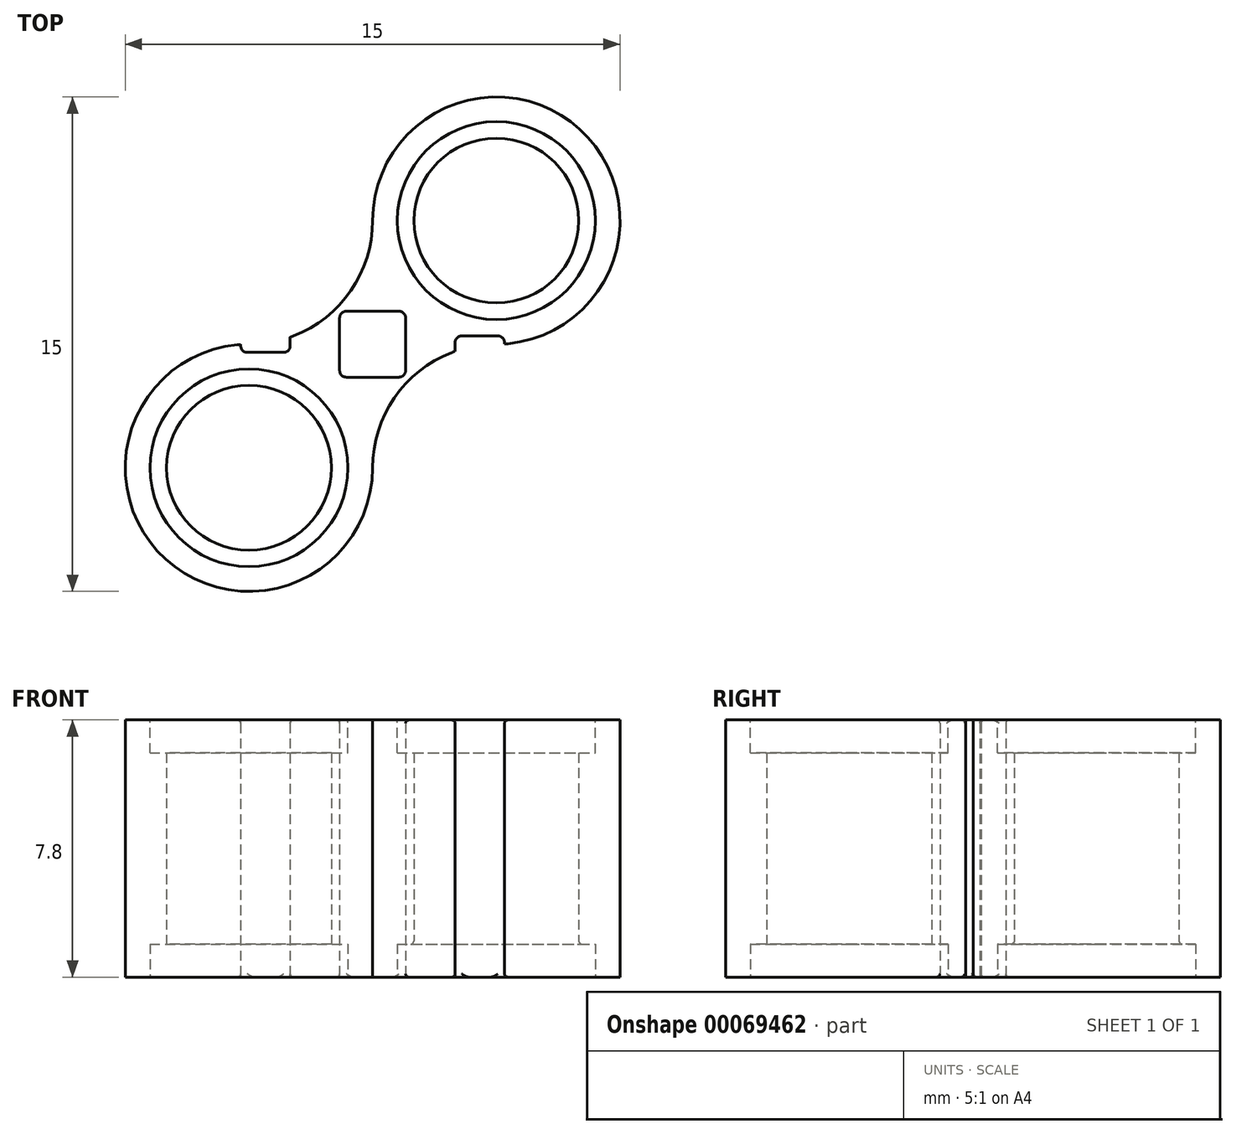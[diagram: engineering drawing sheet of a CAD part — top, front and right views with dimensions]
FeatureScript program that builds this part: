
annotation { "Feature Type Name" : "Feature", "Feature Type Description" : "" }
export const myFeature = defineFeature(function(context is Context, id is Id, definition is map)
    precondition{}
    {
        {
            var Q0;
            Q0=qCreatedBy(makeId("Top.planeOp"),FACE);
            var sketch = newSketch(context, id + "F0", { "sketchPlane" : qUnion([Q0])});
            skLineSegment(sketch, "E0.rect.bottom", {"start": v(7.5, -7.5) * mm, "end": v(-7.5, -7.5) * mm});
            skLineSegment(sketch, "E0.rect.top", {"start": v(7.5, 7.5) * mm, "end": v(-7.5, 7.5) * mm});
            skLineSegment(sketch, "E0.rect.left", {"start": v(7.5, -7.5) * mm, "end": v(7.5, 7.5) * mm});
            skLineSegment(sketch, "E0.rect.right", {"start": v(-7.5, -7.5) * mm, "end": v(-7.5, 7.5) * mm});
            skPoint(sketch, "E0.rect.middle", {"position": v(0, 0) * mm});
            skLineSegment(sketch, "E1.bottom", {"start": v(0, 0) * mm, "end": v(-7.5, 0) * mm, "construction": true});
            skLineSegment(sketch, "E1.top", {"start": v(0, 7.5) * mm, "end": v(-7.5, 7.5) * mm, "construction": true});
            skLineSegment(sketch, "E1.left", {"start": v(0, 0) * mm, "end": v(0, 7.5) * mm, "construction": true});
            skLineSegment(sketch, "E1.right", {"start": v(-7.5, 0) * mm, "end": v(-7.5, 7.5) * mm, "construction": true});
            skLineSegment(sketch, "E2.bottom", {"start": v(0, 0) * mm, "end": v(7.5, 0) * mm, "construction": true});
            skLineSegment(sketch, "E2.top", {"start": v(0, -7.5) * mm, "end": v(7.5, -7.5) * mm, "construction": true});
            skLineSegment(sketch, "E2.right", {"start": v(7.5, 0) * mm, "end": v(7.5, -7.5) * mm, "construction": true});
            skLineSegment(sketch, "E3", {"start": v(7.5, 7.5) * mm, "end": v(0, 0) * mm, "construction": true});
            skLineSegment(sketch, "E4", {"start": v(0, 0) * mm, "end": v(-7.5, -7.5) * mm, "construction": true});
            skLineSegment(sketch, "E5", {"start": v(-7.5, 7.5) * mm, "end": v(0, 0) * mm, "construction": true});
            skLineSegment(sketch, "E6", {"start": v(0, 0) * mm, "end": v(7.5, -7.5) * mm, "construction": true});
            skCircle(sketch, "E7", {"center": v(3.75, 3.75) * mm, "radius": 2.5 * mm});
            skCircle(sketch, "E8.MirrorC", {"center": v(-3.75, 3.75) * mm, "radius": 2.5 * mm});
            skCircle(sketch, "E9.MirrorC", {"center": v(-3.75, -3.75) * mm, "radius": 2.5 * mm});
            skCircle(sketch, "E10.MirrorC", {"center": v(3.75, -3.75) * mm, "radius": 2.5 * mm});
            skCircle(sketch, "E11", {"center": v(3.75, 3.75) * mm, "radius": 3.75 * mm});
            skCircle(sketch, "E12", {"center": v(3.75, 3.75) * mm, "radius": 3 * mm});
            skCircle(sketch, "E13.MirrorC", {"center": v(-3.75, 3.75) * mm, "radius": 3 * mm});
            skCircle(sketch, "E14.MirrorC", {"center": v(-3.75, 3.75) * mm, "radius": 3.75 * mm});
            skCircle(sketch, "E15.MirrorC", {"center": v(-3.75, -3.75) * mm, "radius": 3.75 * mm});
            skCircle(sketch, "E16.MirrorC", {"center": v(-3.75, -3.75) * mm, "radius": 3 * mm});
            skCircle(sketch, "E17.MirrorC", {"center": v(3.75, -3.75) * mm, "radius": 3.75 * mm});
            skCircle(sketch, "E18.MirrorC", {"center": v(3.75, -3.75) * mm, "radius": 3 * mm});
            skLineSegment(sketch, "E19.bottom", {"start": v(-3.75, 7.5) * mm, "end": v(3.75, 7.5) * mm});
            skLineSegment(sketch, "E19.top", {"start": v(-3.75, 3.75) * mm, "end": v(3.75, 3.75) * mm});
            skLineSegment(sketch, "E19.left", {"start": v(-3.75, 7.5) * mm, "end": v(-3.75, 3.75) * mm});
            skLineSegment(sketch, "E19.right", {"start": v(3.75, 7.5) * mm, "end": v(3.75, 3.75) * mm});
            skLineSegment(sketch, "E20.bottom", {"start": v(-7.5, 3.75) * mm, "end": v(-3.75, 3.75) * mm});
            skLineSegment(sketch, "E20.top", {"start": v(-7.5, -3.75) * mm, "end": v(-3.75, -3.75) * mm});
            skLineSegment(sketch, "E20.left", {"start": v(-7.5, 3.75) * mm, "end": v(-7.5, -3.75) * mm});
            skLineSegment(sketch, "E20.right", {"start": v(-3.75, 3.75) * mm, "end": v(-3.75, -3.75) * mm});
            skLineSegment(sketch, "E21.bottom", {"start": v(-3.75, -7.5) * mm, "end": v(3.75, -7.5) * mm});
            skLineSegment(sketch, "E21.top", {"start": v(-3.75, -3.75) * mm, "end": v(3.75, -3.75) * mm});
            skLineSegment(sketch, "E21.left", {"start": v(-3.75, -7.5) * mm, "end": v(-3.75, -3.75) * mm});
            skLineSegment(sketch, "E21.right", {"start": v(3.75, -7.5) * mm, "end": v(3.75, -3.75) * mm});
            skLineSegment(sketch, "E22.bottom", {"start": v(7.5, -3.75) * mm, "end": v(3.75, -3.75) * mm});
            skLineSegment(sketch, "E22.top", {"start": v(7.5, 3.75) * mm, "end": v(3.75, 3.75) * mm});
            skLineSegment(sketch, "E22.left", {"start": v(7.5, -3.75) * mm, "end": v(7.5, 3.75) * mm});
            skLineSegment(sketch, "E22.right", {"start": v(3.75, -3.75) * mm, "end": v(3.75, 3.75) * mm});
            skSolve(sketch);
        }
        {
            var Q0;
            {var subQ0=sQuery(id+"F0.wireOp",EDGE,"E19.bottom");Q0=makeQuery(id+"F0.imprint","IMPRINT",FACE,{"disambiguationData":[TD([[makeQuery(id+"F0.imprint","IMPRINT",EDGE,{"derivedFrom":subQ0}),-1.0]])]});}
            var Q1;
            {var subQ0=sQuery(id+"F0.wireOp",EDGE,"E22.left");Q1=makeQuery(id+"F0.imprint","IMPRINT",FACE,{"disambiguationData":[TD([[makeQuery(id+"F0.imprint","IMPRINT",EDGE,{"derivedFrom":subQ0}),1.0]])]});}
            var Q2;
            {var subQ0=sQuery(id+"F0.wireOp",EDGE,"E20.left");Q2=makeQuery(id+"F0.imprint","IMPRINT",FACE,{"disambiguationData":[TD([[makeQuery(id+"F0.imprint","IMPRINT",EDGE,{"derivedFrom":subQ0}),1.0]])]});}
            var Q3;
            {var subQ0=sQuery(id+"F0.wireOp",EDGE,"E21.bottom");Q3=makeQuery(id+"F0.imprint","IMPRINT",FACE,{"disambiguationData":[TD([[makeQuery(id+"F0.imprint","IMPRINT",EDGE,{"derivedFrom":subQ0}),1.0]])]});}
            var Q4;
            {var subQ0=sQuery(id+"F0.wireOp",EDGE,"E19.right");var subQ5=sQuery(id+"F0.wireOp",EDGE,"E12");var subQ6=makeQuery(id+"F0.imprint","INTERSECT",VERTEX,{"derivedFrom":[subQ5,subQ0]});Q4=makeQuery(id+"F0.imprint","IMPRINT",FACE,{"disambiguationData":[TD([[makeQuery(id+"F0.imprint","IMPRINT",EDGE,{"disambiguationData":[TD([[subQ6,1.0]])],"derivedFrom":subQ5}),-1.0]])]});}
            var Q5;
            {var subQ0=sQuery(id+"F0.wireOp",EDGE,"E19.right");var subQ5=sQuery(id+"F0.wireOp",EDGE,"E12");var subQ6=makeQuery(id+"F0.imprint","INTERSECT",VERTEX,{"derivedFrom":[subQ5,subQ0]});Q5=makeQuery(id+"F0.imprint","IMPRINT",FACE,{"disambiguationData":[TD([[makeQuery(id+"F0.imprint","IMPRINT",EDGE,{"disambiguationData":[TD([[subQ6,-1.0]])],"derivedFrom":subQ5}),-1.0]])]});}
            var Q6;
            {var subQ0=sQuery(id+"F0.wireOp",EDGE,"E22.top");var subQ5=sQuery(id+"F0.wireOp",EDGE,"E12");var subQ7=makeQuery(id+"F0.imprint","INTERSECT",VERTEX,{"derivedFrom":[subQ5,subQ0]});Q6=makeQuery(id+"F0.imprint","IMPRINT",FACE,{"disambiguationData":[TD([[makeQuery(id+"F0.imprint","IMPRINT",EDGE,{"disambiguationData":[TD([[subQ7,1.0]])],"derivedFrom":subQ5}),-1.0]])]});}
            var Q7;
            {var subQ0=sQuery(id+"F0.wireOp",EDGE,"E19.left");var subQ1=sQuery(id+"F0.wireOp",EDGE,"E13.MirrorC");var subQ2=makeQuery(id+"F0.imprint","INTERSECT",VERTEX,{"derivedFrom":[subQ1,subQ0]});Q7=makeQuery(id+"F0.imprint","IMPRINT",FACE,{"disambiguationData":[TD([[makeQuery(id+"F0.imprint","IMPRINT",EDGE,{"disambiguationData":[TD([[subQ2,1.0]])],"derivedFrom":subQ1}),1.0]])]});}
            var Q8;
            {var subQ0=sQuery(id+"F0.wireOp",EDGE,"E19.left");var subQ1=sQuery(id+"F0.wireOp",EDGE,"E13.MirrorC");var subQ2=makeQuery(id+"F0.imprint","INTERSECT",VERTEX,{"derivedFrom":[subQ1,subQ0]});Q8=makeQuery(id+"F0.imprint","IMPRINT",FACE,{"disambiguationData":[TD([[makeQuery(id+"F0.imprint","IMPRINT",EDGE,{"disambiguationData":[TD([[subQ2,-1.0]])],"derivedFrom":subQ1}),1.0]])]});}
            var Q9;
            {var subQ0=sQuery(id+"F0.wireOp",EDGE,"E20.bottom");var subQ1=sQuery(id+"F0.wireOp",EDGE,"E13.MirrorC");var subQ2=makeQuery(id+"F0.imprint","INTERSECT",VERTEX,{"derivedFrom":[subQ1,subQ0]});Q9=makeQuery(id+"F0.imprint","IMPRINT",FACE,{"disambiguationData":[TD([[makeQuery(id+"F0.imprint","IMPRINT",EDGE,{"disambiguationData":[TD([[subQ2,1.0]])],"derivedFrom":subQ1}),1.0]])]});}
            var Q10;
            {var subQ3=sQuery(id+"F0.wireOp",EDGE,"E21.left");var subQ5=sQuery(id+"F0.wireOp",EDGE,"E16.MirrorC");var subQ6=makeQuery(id+"F0.imprint","INTERSECT",VERTEX,{"derivedFrom":[subQ5,subQ3]});Q10=makeQuery(id+"F0.imprint","IMPRINT",FACE,{"disambiguationData":[TD([[makeQuery(id+"F0.imprint","IMPRINT",EDGE,{"disambiguationData":[TD([[subQ6,1.0]])],"derivedFrom":subQ5}),-1.0]])]});}
            var Q11;
            {var subQ0=sQuery(id+"F0.wireOp",EDGE,"E21.left");var subQ5=sQuery(id+"F0.wireOp",EDGE,"E16.MirrorC");var subQ6=makeQuery(id+"F0.imprint","INTERSECT",VERTEX,{"derivedFrom":[subQ5,subQ0]});Q11=makeQuery(id+"F0.imprint","IMPRINT",FACE,{"disambiguationData":[TD([[makeQuery(id+"F0.imprint","IMPRINT",EDGE,{"disambiguationData":[TD([[subQ6,-1.0]])],"derivedFrom":subQ5}),-1.0]])]});}
            var Q12;
            {var subQ0=sQuery(id+"F0.wireOp",EDGE,"E20.top");var subQ5=sQuery(id+"F0.wireOp",EDGE,"E16.MirrorC");var subQ6=makeQuery(id+"F0.imprint","INTERSECT",VERTEX,{"derivedFrom":[subQ5,subQ0]});Q12=makeQuery(id+"F0.imprint","IMPRINT",FACE,{"disambiguationData":[TD([[makeQuery(id+"F0.imprint","IMPRINT",EDGE,{"disambiguationData":[TD([[subQ6,1.0]])],"derivedFrom":subQ5}),-1.0]])]});}
            var Q13;
            {var subQ0=sQuery(id+"F0.wireOp",EDGE,"E21.right");var subQ5=sQuery(id+"F0.wireOp",EDGE,"E18.MirrorC");var subQ6=makeQuery(id+"F0.imprint","INTERSECT",VERTEX,{"derivedFrom":[subQ5,subQ0]});Q13=makeQuery(id+"F0.imprint","IMPRINT",FACE,{"disambiguationData":[TD([[makeQuery(id+"F0.imprint","IMPRINT",EDGE,{"disambiguationData":[TD([[subQ6,1.0]])],"derivedFrom":subQ5}),1.0]])]});}
            var Q14;
            {var subQ0=sQuery(id+"F0.wireOp",EDGE,"E21.right");var subQ5=sQuery(id+"F0.wireOp",EDGE,"E18.MirrorC");var subQ6=makeQuery(id+"F0.imprint","INTERSECT",VERTEX,{"derivedFrom":[subQ5,subQ0]});Q14=makeQuery(id+"F0.imprint","IMPRINT",FACE,{"disambiguationData":[TD([[makeQuery(id+"F0.imprint","IMPRINT",EDGE,{"disambiguationData":[TD([[subQ6,-1.0]])],"derivedFrom":subQ5}),1.0]])]});}
            var Q15;
            {var subQ0=sQuery(id+"F0.wireOp",EDGE,"E22.bottom");var subQ5=sQuery(id+"F0.wireOp",EDGE,"E18.MirrorC");var subQ6=makeQuery(id+"F0.imprint","INTERSECT",VERTEX,{"derivedFrom":[subQ5,subQ0]});Q15=makeQuery(id+"F0.imprint","IMPRINT",FACE,{"disambiguationData":[TD([[makeQuery(id+"F0.imprint","IMPRINT",EDGE,{"disambiguationData":[TD([[subQ6,1.0]])],"derivedFrom":subQ5}),1.0]])]});}
            var Q16;
            {var subQ0=sQuery(id+"F0.wireOp",EDGE,"E19.right");var subQ1=sQuery(id+"F0.wireOp",EDGE,"E7");var subQ2=makeQuery(id+"F0.imprint","INTERSECT",VERTEX,{"derivedFrom":[subQ1,subQ0]});Q16=makeQuery(id+"F0.imprint","IMPRINT",FACE,{"disambiguationData":[TD([[makeQuery(id+"F0.imprint","IMPRINT",EDGE,{"disambiguationData":[TD([[subQ2,1.0]])],"derivedFrom":subQ1}),-1.0]])]});}
            var Q17;
            {var subQ0=sQuery(id+"F0.wireOp",EDGE,"E22.top");var subQ1=sQuery(id+"F0.wireOp",EDGE,"E7");var subQ2=makeQuery(id+"F0.imprint","INTERSECT",VERTEX,{"derivedFrom":[subQ1,subQ0]});Q17=makeQuery(id+"F0.imprint","IMPRINT",FACE,{"disambiguationData":[TD([[makeQuery(id+"F0.imprint","IMPRINT",EDGE,{"disambiguationData":[TD([[subQ2,1.0]])],"derivedFrom":subQ1}),-1.0]])]});}
            var Q18;
            {var subQ0=sQuery(id+"F0.wireOp",EDGE,"E19.top");var subQ1=sQuery(id+"F0.wireOp",EDGE,"E7");var subQ2=makeQuery(id+"F0.imprint","INTERSECT",VERTEX,{"derivedFrom":[subQ1,subQ0]});Q18=makeQuery(id+"F0.imprint","IMPRINT",FACE,{"disambiguationData":[TD([[makeQuery(id+"F0.imprint","IMPRINT",EDGE,{"disambiguationData":[TD([[subQ2,-1.0]])],"derivedFrom":subQ1}),-1.0]])]});}
            var Q19;
            {var subQ0=sQuery(id+"F0.wireOp",EDGE,"E19.right");var subQ1=sQuery(id+"F0.wireOp",EDGE,"E7");var subQ2=makeQuery(id+"F0.imprint","INTERSECT",VERTEX,{"derivedFrom":[subQ1,subQ0]});Q19=makeQuery(id+"F0.imprint","IMPRINT",FACE,{"disambiguationData":[TD([[makeQuery(id+"F0.imprint","IMPRINT",EDGE,{"disambiguationData":[TD([[subQ2,-1.0]])],"derivedFrom":subQ1}),-1.0]])]});}
            var Q20;
            {var subQ0=sQuery(id+"F0.wireOp",EDGE,"E19.top");var subQ5=sQuery(id+"F0.wireOp",EDGE,"E12");var subQ6=makeQuery(id+"F0.imprint","INTERSECT",VERTEX,{"derivedFrom":[subQ5,subQ0]});Q20=makeQuery(id+"F0.imprint","IMPRINT",FACE,{"disambiguationData":[TD([[makeQuery(id+"F0.imprint","IMPRINT",EDGE,{"disambiguationData":[TD([[subQ6,-1.0]])],"derivedFrom":subQ5}),-1.0]])]});}
            var Q21;
            {var subQ0=sQuery(id+"F0.wireOp",EDGE,"E14.MirrorC");var subQ1=sQuery(id+"F0.wireOp",EDGE,"E11");var subQ2=makeQuery(id+"F0.imprint","INTERSECT",VERTEX,{"derivedFrom":[subQ1,subQ0,sQuery(id+"F0.wireOp",EDGE,"E19.top")]});Q21=makeQuery(id+"F0.imprint","IMPRINT",FACE,{"disambiguationData":[TD([[makeQuery(id+"F0.imprint","IMPRINT",EDGE,{"disambiguationData":[TD([[subQ2,-1.0]])],"derivedFrom":subQ1}),-1.0]])]});}
            var Q22;
            {var subQ0=sQuery(id+"F0.wireOp",EDGE,"E20.bottom");var subQ1=sQuery(id+"F0.wireOp",EDGE,"E8.MirrorC");var subQ2=makeQuery(id+"F0.imprint","INTERSECT",VERTEX,{"derivedFrom":[subQ1,subQ0]});Q22=makeQuery(id+"F0.imprint","IMPRINT",FACE,{"disambiguationData":[TD([[makeQuery(id+"F0.imprint","IMPRINT",EDGE,{"disambiguationData":[TD([[subQ2,1.0]])],"derivedFrom":subQ1}),1.0]])]});}
            var Q23;
            {var subQ0=sQuery(id+"F0.wireOp",EDGE,"E19.left");var subQ1=sQuery(id+"F0.wireOp",EDGE,"E8.MirrorC");var subQ2=makeQuery(id+"F0.imprint","INTERSECT",VERTEX,{"derivedFrom":[subQ1,subQ0]});Q23=makeQuery(id+"F0.imprint","IMPRINT",FACE,{"disambiguationData":[TD([[makeQuery(id+"F0.imprint","IMPRINT",EDGE,{"disambiguationData":[TD([[subQ2,1.0]])],"derivedFrom":subQ1}),1.0]])]});}
            var Q24;
            {var subQ0=sQuery(id+"F0.wireOp",EDGE,"E19.left");var subQ1=sQuery(id+"F0.wireOp",EDGE,"E8.MirrorC");var subQ2=makeQuery(id+"F0.imprint","INTERSECT",VERTEX,{"derivedFrom":[subQ1,subQ0]});Q24=makeQuery(id+"F0.imprint","IMPRINT",FACE,{"disambiguationData":[TD([[makeQuery(id+"F0.imprint","IMPRINT",EDGE,{"disambiguationData":[TD([[subQ2,-1.0]])],"derivedFrom":subQ1}),1.0]])]});}
            var Q25;
            {var subQ0=sQuery(id+"F0.wireOp",EDGE,"E19.top");var subQ1=sQuery(id+"F0.wireOp",EDGE,"E8.MirrorC");var subQ2=makeQuery(id+"F0.imprint","INTERSECT",VERTEX,{"derivedFrom":[subQ1,subQ0]});Q25=makeQuery(id+"F0.imprint","IMPRINT",FACE,{"disambiguationData":[TD([[makeQuery(id+"F0.imprint","IMPRINT",EDGE,{"disambiguationData":[TD([[subQ2,-1.0]])],"derivedFrom":subQ1}),1.0]])]});}
            var Q26;
            {var subQ0=sQuery(id+"F0.wireOp",EDGE,"E19.top");var subQ1=sQuery(id+"F0.wireOp",EDGE,"E13.MirrorC");var subQ2=makeQuery(id+"F0.imprint","INTERSECT",VERTEX,{"derivedFrom":[subQ1,subQ0]});Q26=makeQuery(id+"F0.imprint","IMPRINT",FACE,{"disambiguationData":[TD([[makeQuery(id+"F0.imprint","IMPRINT",EDGE,{"disambiguationData":[TD([[subQ2,-1.0]])],"derivedFrom":subQ1}),1.0]])]});}
            var Q27;
            {var subQ3=sQuery(id+"F0.wireOp",EDGE,"E21.top");var subQ5=sQuery(id+"F0.wireOp",EDGE,"E18.MirrorC");var subQ6=makeQuery(id+"F0.imprint","INTERSECT",VERTEX,{"derivedFrom":[subQ5,subQ3]});Q27=makeQuery(id+"F0.imprint","IMPRINT",FACE,{"disambiguationData":[TD([[makeQuery(id+"F0.imprint","IMPRINT",EDGE,{"disambiguationData":[TD([[subQ6,-1.0]])],"derivedFrom":subQ5}),1.0]])]});}
            var Q28;
            {var subQ0=sQuery(id+"F0.wireOp",EDGE,"E21.top");var subQ1=sQuery(id+"F0.wireOp",EDGE,"E10.MirrorC");var subQ2=makeQuery(id+"F0.imprint","INTERSECT",VERTEX,{"derivedFrom":[subQ1,subQ0]});Q28=makeQuery(id+"F0.imprint","IMPRINT",FACE,{"disambiguationData":[TD([[makeQuery(id+"F0.imprint","IMPRINT",EDGE,{"disambiguationData":[TD([[subQ2,-1.0]])],"derivedFrom":subQ1}),1.0]])]});}
            var Q29;
            {var subQ0=sQuery(id+"F0.wireOp",EDGE,"E21.right");var subQ1=sQuery(id+"F0.wireOp",EDGE,"E10.MirrorC");var subQ2=makeQuery(id+"F0.imprint","INTERSECT",VERTEX,{"derivedFrom":[subQ1,subQ0]});Q29=makeQuery(id+"F0.imprint","IMPRINT",FACE,{"disambiguationData":[TD([[makeQuery(id+"F0.imprint","IMPRINT",EDGE,{"disambiguationData":[TD([[subQ2,1.0]])],"derivedFrom":subQ1}),1.0]])]});}
            var Q30;
            {var subQ3=sQuery(id+"F0.wireOp",EDGE,"E21.top");var subQ5=sQuery(id+"F0.wireOp",EDGE,"E16.MirrorC");var subQ6=makeQuery(id+"F0.imprint","INTERSECT",VERTEX,{"derivedFrom":[subQ5,subQ3]});Q30=makeQuery(id+"F0.imprint","IMPRINT",FACE,{"disambiguationData":[TD([[makeQuery(id+"F0.imprint","IMPRINT",EDGE,{"disambiguationData":[TD([[subQ6,-1.0]])],"derivedFrom":subQ5}),-1.0]])]});}
            var Q31;
            {var subQ0=sQuery(id+"F0.wireOp",EDGE,"E21.top");var subQ1=sQuery(id+"F0.wireOp",EDGE,"E9.MirrorC");var subQ2=makeQuery(id+"F0.imprint","INTERSECT",VERTEX,{"derivedFrom":[subQ1,subQ0]});Q31=makeQuery(id+"F0.imprint","IMPRINT",FACE,{"disambiguationData":[TD([[makeQuery(id+"F0.imprint","IMPRINT",EDGE,{"disambiguationData":[TD([[subQ2,-1.0]])],"derivedFrom":subQ1}),-1.0]])]});}
            var Q32;
            {var subQ0=sQuery(id+"F0.wireOp",EDGE,"E20.top");var subQ1=sQuery(id+"F0.wireOp",EDGE,"E9.MirrorC");var subQ2=makeQuery(id+"F0.imprint","INTERSECT",VERTEX,{"derivedFrom":[subQ1,subQ0]});Q32=makeQuery(id+"F0.imprint","IMPRINT",FACE,{"disambiguationData":[TD([[makeQuery(id+"F0.imprint","IMPRINT",EDGE,{"disambiguationData":[TD([[subQ2,1.0]])],"derivedFrom":subQ1}),-1.0]])]});}
            var Q33;
            {var subQ0=sQuery(id+"F0.wireOp",EDGE,"E21.left");var subQ1=sQuery(id+"F0.wireOp",EDGE,"E9.MirrorC");var subQ2=makeQuery(id+"F0.imprint","INTERSECT",VERTEX,{"derivedFrom":[subQ1,subQ0]});Q33=makeQuery(id+"F0.imprint","IMPRINT",FACE,{"disambiguationData":[TD([[makeQuery(id+"F0.imprint","IMPRINT",EDGE,{"disambiguationData":[TD([[subQ2,1.0]])],"derivedFrom":subQ1}),-1.0]])]});}
            var Q34;
            {var subQ0=sQuery(id+"F0.wireOp",EDGE,"E21.left");var subQ1=sQuery(id+"F0.wireOp",EDGE,"E9.MirrorC");var subQ2=makeQuery(id+"F0.imprint","INTERSECT",VERTEX,{"derivedFrom":[subQ1,subQ0]});Q34=makeQuery(id+"F0.imprint","IMPRINT",FACE,{"disambiguationData":[TD([[makeQuery(id+"F0.imprint","IMPRINT",EDGE,{"disambiguationData":[TD([[subQ2,-1.0]])],"derivedFrom":subQ1}),-1.0]])]});}
            var Q35;
            {var subQ0=sQuery(id+"F0.wireOp",EDGE,"E21.right");var subQ1=sQuery(id+"F0.wireOp",EDGE,"E10.MirrorC");var subQ2=makeQuery(id+"F0.imprint","INTERSECT",VERTEX,{"derivedFrom":[subQ1,subQ0]});Q35=makeQuery(id+"F0.imprint","IMPRINT",FACE,{"disambiguationData":[TD([[makeQuery(id+"F0.imprint","IMPRINT",EDGE,{"disambiguationData":[TD([[subQ2,-1.0]])],"derivedFrom":subQ1}),1.0]])]});}
            var Q36;
            {var subQ0=sQuery(id+"F0.wireOp",EDGE,"E22.bottom");var subQ1=sQuery(id+"F0.wireOp",EDGE,"E10.MirrorC");var subQ2=makeQuery(id+"F0.imprint","INTERSECT",VERTEX,{"derivedFrom":[subQ1,subQ0]});Q36=makeQuery(id+"F0.imprint","IMPRINT",FACE,{"disambiguationData":[TD([[makeQuery(id+"F0.imprint","IMPRINT",EDGE,{"disambiguationData":[TD([[subQ2,1.0]])],"derivedFrom":subQ1}),1.0]])]});}
            extrude(context, id + "F1", {"entities" : qUnion([Q0, Q1, Q2, Q3, Q4, Q5, Q6, Q7, Q8, Q9, Q10, Q11, Q12, Q13, Q14, Q15, Q16, Q17, Q18, Q19, Q20, Q21, Q22, Q23, Q24, Q25, Q26, Q27, Q28, Q29, Q30, Q31, Q32, Q33, Q34, Q35, Q36]), "depth" : 7.8 * mm});
        }
        {
            var Q0;
            Q0=makeQuery(id+"F1.opExtrude","CAP_FACE",FACE,{"disambiguationData":[OSD([sQuery(id+"F0.wireOp",EDGE,"E7"),sQuery(id+"F0.wireOp",EDGE,"E8.MirrorC"),sQuery(id+"F0.wireOp",EDGE,"E9.MirrorC"),sQuery(id+"F0.wireOp",EDGE,"E10.MirrorC"),sQuery(id+"F0.wireOp",EDGE,"E11"),sQuery(id+"F0.wireOp",EDGE,"E14.MirrorC"),sQuery(id+"F0.wireOp",EDGE,"E15.MirrorC"),sQuery(id+"F0.wireOp",EDGE,"E17.MirrorC"),sQuery(id+"F0.wireOp",EDGE,"E19.bottom"),sQuery(id+"F0.wireOp",EDGE,"E20.left"),sQuery(id+"F0.wireOp",EDGE,"E21.bottom"),sQuery(id+"F0.wireOp",EDGE,"E22.left")])],"isStart":true});
            var sketch = newSketch(context, id + "F2", { "sketchPlane" : qUnion([Q0])});
            skCircle(sketch, "E23.0", {"center": v(-3.75, 3.75) * mm, "radius": 2.5 * mm});
            skCircle(sketch, "E24.0", {"center": v(-3.75, 3.75) * mm, "radius": 3 * mm});
            skLineSegment(sketch, "E25", {"start": v(0, 0) * mm, "end": v(-7.5, 0) * mm, "construction": true});
            skLineSegment(sketch, "E26", {"start": v(0, 7.5) * mm, "end": v(0, -7.5) * mm, "construction": true});
            skCircle(sketch, "E27.MirrorC", {"center": v(-3.75, -3.75) * mm, "radius": 3 * mm});
            skCircle(sketch, "E28.MirrorC", {"center": v(3.75, -3.75) * mm, "radius": 3 * mm});
            skCircle(sketch, "E29.MirrorC", {"center": v(3.75, 3.75) * mm, "radius": 3 * mm});
            skSolve(sketch);
        }
        {
            var Q0;
            Q0 = qSketchRegion(id + "F2", true);
            extrude(context, id + "F3", {"entities" : qUnion([Q0]), "operationType" : NewBodyOperationType.REMOVE, "oppositeDirection" : true, "depth" : 1 * mm});
        }
        {
            var Q0;
            Q0=makeQuery(id+"F1.opExtrude","CAP_FACE",FACE,{"disambiguationData":[OSD([sQuery(id+"F0.wireOp",EDGE,"E7"),sQuery(id+"F0.wireOp",EDGE,"E8.MirrorC"),sQuery(id+"F0.wireOp",EDGE,"E9.MirrorC"),sQuery(id+"F0.wireOp",EDGE,"E10.MirrorC"),sQuery(id+"F0.wireOp",EDGE,"E11"),sQuery(id+"F0.wireOp",EDGE,"E14.MirrorC"),sQuery(id+"F0.wireOp",EDGE,"E15.MirrorC"),sQuery(id+"F0.wireOp",EDGE,"E17.MirrorC"),sQuery(id+"F0.wireOp",EDGE,"E19.bottom"),sQuery(id+"F0.wireOp",EDGE,"E20.left"),sQuery(id+"F0.wireOp",EDGE,"E21.bottom"),sQuery(id+"F0.wireOp",EDGE,"E22.left")])],"isStart":true});
            cPlane(context, id + "F4", {"entities" : qUnion([Q0]), "cplaneType" : CPlaneType.OFFSET, "offset" : 3.9 * mm, "oppositeDirection" : true, "width" : 150 * mm, "height" : 150 * mm});
        }
        {
            var Q0;
            Q0=makeQuery(id+"F1.opExtrude","SWEPT_BODY",BODY,{"disambiguationData":[OSD([sQuery(id+"F0.wireOp",EDGE,"E7"),sQuery(id+"F0.wireOp",EDGE,"E8.MirrorC"),sQuery(id+"F0.wireOp",EDGE,"E9.MirrorC"),sQuery(id+"F0.wireOp",EDGE,"E10.MirrorC"),sQuery(id+"F0.wireOp",EDGE,"E11"),sQuery(id+"F0.wireOp",EDGE,"E14.MirrorC"),sQuery(id+"F0.wireOp",EDGE,"E15.MirrorC"),sQuery(id+"F0.wireOp",EDGE,"E17.MirrorC"),sQuery(id+"F0.wireOp",EDGE,"E19.bottom"),sQuery(id+"F0.wireOp",EDGE,"E20.left"),sQuery(id+"F0.wireOp",EDGE,"E21.bottom"),sQuery(id+"F0.wireOp",EDGE,"E22.left")])]});
            var Q1;
            Q1=qCreatedBy(id+"F4.planeOp",FACE);
            mirror(context, id + "F5", {"operationType" : NewBodyOperationType.INTERSECT, "entities" : qUnion([Q0]), "mirrorPlane" : qUnion([Q1])});
        }
        {
            var Q0;
            Q0=makeQuery(id+"F1.opExtrude","CAP_FACE",FACE,{"disambiguationData":[OSD([sQuery(id+"F0.wireOp",EDGE,"E7"),sQuery(id+"F0.wireOp",EDGE,"E8.MirrorC"),sQuery(id+"F0.wireOp",EDGE,"E9.MirrorC"),sQuery(id+"F0.wireOp",EDGE,"E10.MirrorC"),sQuery(id+"F0.wireOp",EDGE,"E11"),sQuery(id+"F0.wireOp",EDGE,"E14.MirrorC"),sQuery(id+"F0.wireOp",EDGE,"E15.MirrorC"),sQuery(id+"F0.wireOp",EDGE,"E17.MirrorC"),sQuery(id+"F0.wireOp",EDGE,"E19.bottom"),sQuery(id+"F0.wireOp",EDGE,"E20.left"),sQuery(id+"F0.wireOp",EDGE,"E21.bottom"),sQuery(id+"F0.wireOp",EDGE,"E22.left")])],"isStart":true});
            var sketch = newSketch(context, id + "F6", { "sketchPlane" : qUnion([Q0])});
            skLineSegment(sketch, "E30.rect.bottom", {"start": v(2.5, -1) * mm, "end": v(-2.5, -1) * mm});
            skLineSegment(sketch, "E30.rect.top", {"start": v(2.5, 1) * mm, "end": v(-2.5, 1) * mm});
            skLineSegment(sketch, "E30.rect.left", {"start": v(2.5, -1) * mm, "end": v(2.5, 1) * mm});
            skLineSegment(sketch, "E30.rect.right", {"start": v(-2.5, -1) * mm, "end": v(-2.5, 1) * mm});
            skPoint(sketch, "E30.rect.middle", {"position": v(0, 0) * mm});
            skLineSegment(sketch, "E31.rect.bottom", {"start": v(-1, 2.5) * mm, "end": v(1, 2.5) * mm});
            skLineSegment(sketch, "E31.rect.top", {"start": v(-1, -2.5) * mm, "end": v(1, -2.5) * mm});
            skLineSegment(sketch, "E31.rect.left", {"start": v(-1, 2.5) * mm, "end": v(-1, -2.5) * mm});
            skLineSegment(sketch, "E31.rect.right", {"start": v(1, 2.5) * mm, "end": v(1, -2.5) * mm});
            skLineSegment(sketch, "E32.rect.bottom", {"start": v(4, -0.25) * mm, "end": v(-4, -0.25) * mm});
            skLineSegment(sketch, "E32.rect.top", {"start": v(4, 0.25) * mm, "end": v(-4, 0.25) * mm});
            skLineSegment(sketch, "E32.rect.left", {"start": v(4, -0.25) * mm, "end": v(4, 0.25) * mm});
            skLineSegment(sketch, "E32.rect.right", {"start": v(-4, -0.25) * mm, "end": v(-4, 0.25) * mm});
            skSolve(sketch);
        }
        {
            var Q0;
            {var subQ0=sQuery(id+"F6.wireOp",EDGE,"E30.rect.right");Q0=makeQuery(id+"F6.imprint","IMPRINT",FACE,{"disambiguationData":[TD([[makeQuery(id+"F6.imprint","IMPRINT",EDGE,{"derivedFrom":subQ0}),-1.0]])]});}
            var Q1;
            {var subQ5=sQuery(id+"F6.wireOp",EDGE,"E31.rect.bottom");Q1=makeQuery(id+"F6.imprint","IMPRINT",FACE,{"disambiguationData":[TD([[makeQuery(id+"F6.imprint","IMPRINT",EDGE,{"derivedFrom":subQ5}),-1.0]])]});}
            var Q2;
            {var subQ0=sQuery(id+"F6.wireOp",EDGE,"E30.rect.left");Q2=makeQuery(id+"F6.imprint","IMPRINT",FACE,{"disambiguationData":[TD([[makeQuery(id+"F6.imprint","IMPRINT",EDGE,{"derivedFrom":subQ0}),1.0]])]});}
            var Q3;
            {var subQ5=sQuery(id+"F6.wireOp",EDGE,"E31.rect.top");Q3=makeQuery(id+"F6.imprint","IMPRINT",FACE,{"disambiguationData":[TD([[makeQuery(id+"F6.imprint","IMPRINT",EDGE,{"derivedFrom":subQ5}),1.0]])]});}
            var Q4;
            {var subQ0=sQuery(id+"F6.wireOp",EDGE,"E31.rect.right");var subQ1=sQuery(id+"F6.wireOp",EDGE,"E30.rect.bottom");var subQ2=makeQuery(id+"F6.imprint","INTERSECT",VERTEX,{"derivedFrom":[subQ1,subQ0]});Q4=makeQuery(id+"F6.imprint","IMPRINT",FACE,{"disambiguationData":[TD([[makeQuery(id+"F6.imprint","IMPRINT",EDGE,{"disambiguationData":[TD([[subQ2,-1.0]])],"derivedFrom":subQ1}),-1.0]])]});}
            var Q5;
            {var subQ5=sQuery(id+"F6.wireOp",EDGE,"E32.rect.left");Q5=makeQuery(id+"F6.imprint","IMPRINT",FACE,{"disambiguationData":[TD([[makeQuery(id+"F6.imprint","IMPRINT",EDGE,{"derivedFrom":subQ5}),1.0]])]});}
            var Q6;
            {var subQ0=sQuery(id+"F6.wireOp",EDGE,"E32.rect.top");var subQ1=sQuery(id+"F6.wireOp",EDGE,"E31.rect.left");var subQ2=makeQuery(id+"F6.imprint","INTERSECT",VERTEX,{"derivedFrom":[subQ1,subQ0]});Q6=makeQuery(id+"F6.imprint","IMPRINT",FACE,{"disambiguationData":[TD([[makeQuery(id+"F6.imprint","IMPRINT",EDGE,{"disambiguationData":[TD([[subQ2,-1.0]])],"derivedFrom":subQ1}),1.0]])]});}
            var Q7;
            {var subQ5=sQuery(id+"F6.wireOp",EDGE,"E32.rect.right");Q7=makeQuery(id+"F6.imprint","IMPRINT",FACE,{"disambiguationData":[TD([[makeQuery(id+"F6.imprint","IMPRINT",EDGE,{"derivedFrom":subQ5}),-1.0]])]});}
            var Q8;
            {var subQ0=sQuery(id+"F6.wireOp",EDGE,"E31.rect.right");var subQ1=sQuery(id+"F6.wireOp",EDGE,"E30.rect.top");var subQ2=makeQuery(id+"F6.imprint","INTERSECT",VERTEX,{"derivedFrom":[subQ1,subQ0]});Q8=makeQuery(id+"F6.imprint","IMPRINT",FACE,{"disambiguationData":[TD([[makeQuery(id+"F6.imprint","IMPRINT",EDGE,{"disambiguationData":[TD([[subQ2,-1.0]])],"derivedFrom":subQ1}),1.0]])]});}
            extrude(context, id + "F7", {"entities" : qUnion([Q0, Q1, Q2, Q3, Q4, Q5, Q6, Q7, Q8]), "operationType" : NewBodyOperationType.REMOVE, "oppositeDirection" : true, "depth" : 25 * mm});
        }
        {
            var Q0;
            Q0=makeQuery(id+"F7.boolean.opBoolean","COPY",EDGE,{"derivedFrom":makeQuery(id+"F7.opExtrude","SWEPT_EDGE",EDGE,{"disambiguationData":[OSD([sQuery(id+"F6.wireOp",EDGE,"E30.rect.bottom"),sQuery(id+"F6.wireOp",EDGE,"E30.rect.left")])]})});
            var Q1;
            Q1=makeQuery(id+"F7.boolean.opBoolean","COPY",EDGE,{"derivedFrom":makeQuery(id+"F7.opExtrude","SWEPT_EDGE",EDGE,{"disambiguationData":[OSD([sQuery(id+"F6.wireOp",EDGE,"E31.rect.top"),sQuery(id+"F6.wireOp",EDGE,"E31.rect.right")])]})});
            var Q2;
            Q2=makeQuery(id+"F7.boolean.opBoolean","COPY",EDGE,{"derivedFrom":makeQuery(id+"F7.opExtrude","SWEPT_EDGE",EDGE,{"disambiguationData":[OSD([sQuery(id+"F6.wireOp",EDGE,"E30.rect.top"),sQuery(id+"F6.wireOp",EDGE,"E30.rect.left")])]})});
            var Q3;
            Q3=makeQuery(id+"F7.boolean.opBoolean","COPY",EDGE,{"derivedFrom":makeQuery(id+"F7.opExtrude","SWEPT_EDGE",EDGE,{"disambiguationData":[OSD([sQuery(id+"F6.wireOp",EDGE,"E31.rect.bottom"),sQuery(id+"F6.wireOp",EDGE,"E31.rect.right")])]})});
            var Q4;
            Q4=makeQuery(id+"F7.boolean.opBoolean","COPY",EDGE,{"derivedFrom":makeQuery(id+"F7.opExtrude","SWEPT_EDGE",EDGE,{"disambiguationData":[OSD([sQuery(id+"F6.wireOp",EDGE,"E31.rect.bottom"),sQuery(id+"F6.wireOp",EDGE,"E31.rect.left")])]})});
            var Q5;
            Q5=makeQuery(id+"F7.boolean.opBoolean","COPY",EDGE,{"derivedFrom":makeQuery(id+"F7.opExtrude","SWEPT_EDGE",EDGE,{"disambiguationData":[OSD([sQuery(id+"F6.wireOp",EDGE,"E30.rect.top"),sQuery(id+"F6.wireOp",EDGE,"E30.rect.right")])]})});
            var Q6;
            Q6=makeQuery(id+"F7.boolean.opBoolean","COPY",EDGE,{"derivedFrom":makeQuery(id+"F7.opExtrude","SWEPT_EDGE",EDGE,{"disambiguationData":[OSD([sQuery(id+"F6.wireOp",EDGE,"E30.rect.bottom"),sQuery(id+"F6.wireOp",EDGE,"E30.rect.right")])]})});
            var Q7;
            Q7=makeQuery(id+"F7.boolean.opBoolean","COPY",EDGE,{"derivedFrom":makeQuery(id+"F7.opExtrude","SWEPT_EDGE",EDGE,{"disambiguationData":[OSD([sQuery(id+"F6.wireOp",EDGE,"E31.rect.top"),sQuery(id+"F6.wireOp",EDGE,"E31.rect.left")])]})});
            var Q8;
            Q8=makeQuery(id+"F7.boolean.opBoolean","COPY",EDGE,{"derivedFrom":makeQuery(id+"F7.opExtrude","SWEPT_EDGE",EDGE,{"disambiguationData":[OSD([sQuery(id+"F6.wireOp",EDGE,"E32.rect.bottom"),sQuery(id+"F6.wireOp",EDGE,"E32.rect.right")])]})});
            var Q9;
            Q9=makeQuery(id+"F7.boolean.opBoolean","COPY",EDGE,{"derivedFrom":makeQuery(id+"F7.opExtrude","SWEPT_EDGE",EDGE,{"disambiguationData":[OSD([sQuery(id+"F6.wireOp",EDGE,"E32.rect.top"),sQuery(id+"F6.wireOp",EDGE,"E32.rect.right")])]})});
            var Q10;
            Q10=makeQuery(id+"F7.boolean.opBoolean","COPY",EDGE,{"derivedFrom":makeQuery(id+"F7.opExtrude","SWEPT_EDGE",EDGE,{"disambiguationData":[OSD([sQuery(id+"F6.wireOp",EDGE,"E32.rect.top"),sQuery(id+"F6.wireOp",EDGE,"E32.rect.left")])]})});
            var Q11;
            Q11=makeQuery(id+"F7.boolean.opBoolean","COPY",EDGE,{"derivedFrom":makeQuery(id+"F7.opExtrude","SWEPT_EDGE",EDGE,{"disambiguationData":[OSD([sQuery(id+"F6.wireOp",EDGE,"E32.rect.bottom"),sQuery(id+"F6.wireOp",EDGE,"E32.rect.left")])]})});
            fillet(context, id + "F8", {"entities" : qUnion([Q0, Q1, Q2, Q3, Q4, Q5, Q6, Q7, Q8, Q9, Q10, Q11]), "radius" : 0.2 * mm, "tangentPropagation" : true, "allowEdgeOverflow" : false});
        }
        {
            var Q0;
            Q0=makeQuery(id+"F7.boolean.opBoolean","COPY",EDGE,{"derivedFrom":makeQuery(id+"F7.opExtrude","CAP_EDGE",EDGE,{"disambiguationData":[OSD([sQuery(id+"F6.wireOp",EDGE,"E31.rect.bottom")])],"isStart":true})});
            var Q1;
            {var subQ0=sQuery(id+"F6.wireOp",EDGE,"E31.rect.left");Q1=makeQuery(id+"F7.boolean.opBoolean","COPY",EDGE,{"derivedFrom":makeQuery(id+"F7.opExtrude","CAP_EDGE",EDGE,{"disambiguationData":[OSD([subQ0]),TDD([makeQuery(id+"F6.imprint","IMPRINT",EDGE,{"disambiguationData":[TD([[makeQuery(id+"F6.imprint","INTERSECT",VERTEX,{"derivedFrom":[sQuery(id+"F6.wireOp",EDGE,"E31.rect.bottom"),subQ0]}),-1.0]])],"derivedFrom":subQ0})])],"isStart":true})});}
            var Q2;
            Q2=makeQuery(id+"F8.opFillet","BLEND_EDGE",EDGE,{"blendedFrom":[makeQuery(id+"F7.boolean.opBoolean","COPY",EDGE,{"derivedFrom":makeQuery(id+"F7.opExtrude","SWEPT_EDGE",EDGE,{"disambiguationData":[OSD([sQuery(id+"F6.wireOp",EDGE,"E31.rect.bottom"),sQuery(id+"F6.wireOp",EDGE,"E31.rect.left")])]})}),makeQuery(id+"F1.opExtrude","CAP_FACE",FACE,{"disambiguationData":[OSD([sQuery(id+"F0.wireOp",EDGE,"E7"),sQuery(id+"F0.wireOp",EDGE,"E8.MirrorC"),sQuery(id+"F0.wireOp",EDGE,"E9.MirrorC"),sQuery(id+"F0.wireOp",EDGE,"E10.MirrorC"),sQuery(id+"F0.wireOp",EDGE,"E11"),sQuery(id+"F0.wireOp",EDGE,"E14.MirrorC"),sQuery(id+"F0.wireOp",EDGE,"E15.MirrorC"),sQuery(id+"F0.wireOp",EDGE,"E17.MirrorC"),sQuery(id+"F0.wireOp",EDGE,"E19.bottom"),sQuery(id+"F0.wireOp",EDGE,"E20.left"),sQuery(id+"F0.wireOp",EDGE,"E21.bottom"),sQuery(id+"F0.wireOp",EDGE,"E22.left")])],"isStart":true})],"blendedInto":[makeQuery(id+"F1.opExtrude","CAP_FACE",FACE,{"disambiguationData":[OSD([sQuery(id+"F0.wireOp",EDGE,"E7"),sQuery(id+"F0.wireOp",EDGE,"E8.MirrorC"),sQuery(id+"F0.wireOp",EDGE,"E9.MirrorC"),sQuery(id+"F0.wireOp",EDGE,"E10.MirrorC"),sQuery(id+"F0.wireOp",EDGE,"E11"),sQuery(id+"F0.wireOp",EDGE,"E14.MirrorC"),sQuery(id+"F0.wireOp",EDGE,"E15.MirrorC"),sQuery(id+"F0.wireOp",EDGE,"E17.MirrorC"),sQuery(id+"F0.wireOp",EDGE,"E19.bottom"),sQuery(id+"F0.wireOp",EDGE,"E20.left"),sQuery(id+"F0.wireOp",EDGE,"E21.bottom"),sQuery(id+"F0.wireOp",EDGE,"E22.left")])],"isStart":true})]});
            var Q3;
            Q3=makeQuery(id+"F8.opFillet","BLEND_EDGE",EDGE,{"blendedFrom":[makeQuery(id+"F7.boolean.opBoolean","COPY",EDGE,{"derivedFrom":makeQuery(id+"F7.opExtrude","SWEPT_EDGE",EDGE,{"disambiguationData":[OSD([sQuery(id+"F6.wireOp",EDGE,"E31.rect.bottom"),sQuery(id+"F6.wireOp",EDGE,"E31.rect.right")])]})}),makeQuery(id+"F1.opExtrude","CAP_FACE",FACE,{"disambiguationData":[OSD([sQuery(id+"F0.wireOp",EDGE,"E7"),sQuery(id+"F0.wireOp",EDGE,"E8.MirrorC"),sQuery(id+"F0.wireOp",EDGE,"E9.MirrorC"),sQuery(id+"F0.wireOp",EDGE,"E10.MirrorC"),sQuery(id+"F0.wireOp",EDGE,"E11"),sQuery(id+"F0.wireOp",EDGE,"E14.MirrorC"),sQuery(id+"F0.wireOp",EDGE,"E15.MirrorC"),sQuery(id+"F0.wireOp",EDGE,"E17.MirrorC"),sQuery(id+"F0.wireOp",EDGE,"E19.bottom"),sQuery(id+"F0.wireOp",EDGE,"E20.left"),sQuery(id+"F0.wireOp",EDGE,"E21.bottom"),sQuery(id+"F0.wireOp",EDGE,"E22.left")])],"isStart":true})],"blendedInto":[makeQuery(id+"F1.opExtrude","CAP_FACE",FACE,{"disambiguationData":[OSD([sQuery(id+"F0.wireOp",EDGE,"E7"),sQuery(id+"F0.wireOp",EDGE,"E8.MirrorC"),sQuery(id+"F0.wireOp",EDGE,"E9.MirrorC"),sQuery(id+"F0.wireOp",EDGE,"E10.MirrorC"),sQuery(id+"F0.wireOp",EDGE,"E11"),sQuery(id+"F0.wireOp",EDGE,"E14.MirrorC"),sQuery(id+"F0.wireOp",EDGE,"E15.MirrorC"),sQuery(id+"F0.wireOp",EDGE,"E17.MirrorC"),sQuery(id+"F0.wireOp",EDGE,"E19.bottom"),sQuery(id+"F0.wireOp",EDGE,"E20.left"),sQuery(id+"F0.wireOp",EDGE,"E21.bottom"),sQuery(id+"F0.wireOp",EDGE,"E22.left")])],"isStart":true})]});
            var Q4;
            {var subQ0=sQuery(id+"F6.wireOp",EDGE,"E31.rect.right");Q4=makeQuery(id+"F7.boolean.opBoolean","COPY",EDGE,{"derivedFrom":makeQuery(id+"F7.opExtrude","CAP_EDGE",EDGE,{"disambiguationData":[OSD([subQ0]),TDD([makeQuery(id+"F6.imprint","IMPRINT",EDGE,{"disambiguationData":[TD([[makeQuery(id+"F6.imprint","INTERSECT",VERTEX,{"derivedFrom":[sQuery(id+"F6.wireOp",EDGE,"E31.rect.bottom"),subQ0]}),-1.0]])],"derivedFrom":subQ0})])],"isStart":true})});}
            var Q5;
            {var subQ0=sQuery(id+"F6.wireOp",EDGE,"E30.rect.top");Q5=makeQuery(id+"F7.boolean.opBoolean","COPY",EDGE,{"derivedFrom":makeQuery(id+"F7.opExtrude","CAP_EDGE",EDGE,{"disambiguationData":[OSD([subQ0]),TDD([makeQuery(id+"F6.imprint","IMPRINT",EDGE,{"disambiguationData":[TD([[makeQuery(id+"F6.imprint","INTERSECT",VERTEX,{"derivedFrom":[subQ0,sQuery(id+"F6.wireOp",EDGE,"E30.rect.left")]}),-1.0]])],"derivedFrom":subQ0})])],"isStart":true})});}
            var Q6;
            Q6=makeQuery(id+"F8.opFillet","BLEND_EDGE",EDGE,{"blendedFrom":[makeQuery(id+"F7.boolean.opBoolean","COPY",EDGE,{"derivedFrom":makeQuery(id+"F7.opExtrude","SWEPT_EDGE",EDGE,{"disambiguationData":[OSD([sQuery(id+"F6.wireOp",EDGE,"E30.rect.top"),sQuery(id+"F6.wireOp",EDGE,"E30.rect.left")])]})}),makeQuery(id+"F1.opExtrude","CAP_FACE",FACE,{"disambiguationData":[OSD([sQuery(id+"F0.wireOp",EDGE,"E7"),sQuery(id+"F0.wireOp",EDGE,"E8.MirrorC"),sQuery(id+"F0.wireOp",EDGE,"E9.MirrorC"),sQuery(id+"F0.wireOp",EDGE,"E10.MirrorC"),sQuery(id+"F0.wireOp",EDGE,"E11"),sQuery(id+"F0.wireOp",EDGE,"E14.MirrorC"),sQuery(id+"F0.wireOp",EDGE,"E15.MirrorC"),sQuery(id+"F0.wireOp",EDGE,"E17.MirrorC"),sQuery(id+"F0.wireOp",EDGE,"E19.bottom"),sQuery(id+"F0.wireOp",EDGE,"E20.left"),sQuery(id+"F0.wireOp",EDGE,"E21.bottom"),sQuery(id+"F0.wireOp",EDGE,"E22.left")])],"isStart":true})],"blendedInto":[makeQuery(id+"F1.opExtrude","CAP_FACE",FACE,{"disambiguationData":[OSD([sQuery(id+"F0.wireOp",EDGE,"E7"),sQuery(id+"F0.wireOp",EDGE,"E8.MirrorC"),sQuery(id+"F0.wireOp",EDGE,"E9.MirrorC"),sQuery(id+"F0.wireOp",EDGE,"E10.MirrorC"),sQuery(id+"F0.wireOp",EDGE,"E11"),sQuery(id+"F0.wireOp",EDGE,"E14.MirrorC"),sQuery(id+"F0.wireOp",EDGE,"E15.MirrorC"),sQuery(id+"F0.wireOp",EDGE,"E17.MirrorC"),sQuery(id+"F0.wireOp",EDGE,"E19.bottom"),sQuery(id+"F0.wireOp",EDGE,"E20.left"),sQuery(id+"F0.wireOp",EDGE,"E21.bottom"),sQuery(id+"F0.wireOp",EDGE,"E22.left")])],"isStart":true})]});
            var Q7;
            {var subQ0=sQuery(id+"F6.wireOp",EDGE,"E30.rect.left");Q7=makeQuery(id+"F7.boolean.opBoolean","COPY",EDGE,{"derivedFrom":makeQuery(id+"F7.opExtrude","CAP_EDGE",EDGE,{"disambiguationData":[OSD([subQ0]),TDD([makeQuery(id+"F6.imprint","IMPRINT",EDGE,{"disambiguationData":[TD([[makeQuery(id+"F6.imprint","INTERSECT",VERTEX,{"derivedFrom":[sQuery(id+"F6.wireOp",EDGE,"E30.rect.top"),subQ0]}),1.0]])],"derivedFrom":subQ0})])],"isStart":true})});}
            var Q8;
            {var subQ0=sQuery(id+"F6.wireOp",EDGE,"E32.rect.top");Q8=makeQuery(id+"F7.boolean.opBoolean","COPY",EDGE,{"derivedFrom":makeQuery(id+"F7.opExtrude","CAP_EDGE",EDGE,{"disambiguationData":[OSD([subQ0]),TDD([makeQuery(id+"F6.imprint","IMPRINT",EDGE,{"disambiguationData":[TD([[makeQuery(id+"F6.imprint","INTERSECT",VERTEX,{"derivedFrom":[subQ0,sQuery(id+"F6.wireOp",EDGE,"E32.rect.left")]}),-1.0]])],"derivedFrom":subQ0})])],"isStart":true})});}
            var Q9;
            Q9=makeQuery(id+"F8.opFillet","BLEND_EDGE",EDGE,{"blendedFrom":[makeQuery(id+"F7.boolean.opBoolean","COPY",EDGE,{"derivedFrom":makeQuery(id+"F7.opExtrude","SWEPT_EDGE",EDGE,{"disambiguationData":[OSD([sQuery(id+"F6.wireOp",EDGE,"E32.rect.top"),sQuery(id+"F6.wireOp",EDGE,"E32.rect.left")])]})}),makeQuery(id+"F1.opExtrude","CAP_FACE",FACE,{"disambiguationData":[OSD([sQuery(id+"F0.wireOp",EDGE,"E7"),sQuery(id+"F0.wireOp",EDGE,"E8.MirrorC"),sQuery(id+"F0.wireOp",EDGE,"E9.MirrorC"),sQuery(id+"F0.wireOp",EDGE,"E10.MirrorC"),sQuery(id+"F0.wireOp",EDGE,"E11"),sQuery(id+"F0.wireOp",EDGE,"E14.MirrorC"),sQuery(id+"F0.wireOp",EDGE,"E15.MirrorC"),sQuery(id+"F0.wireOp",EDGE,"E17.MirrorC"),sQuery(id+"F0.wireOp",EDGE,"E19.bottom"),sQuery(id+"F0.wireOp",EDGE,"E20.left"),sQuery(id+"F0.wireOp",EDGE,"E21.bottom"),sQuery(id+"F0.wireOp",EDGE,"E22.left")])],"isStart":true})],"blendedInto":[makeQuery(id+"F1.opExtrude","CAP_FACE",FACE,{"disambiguationData":[OSD([sQuery(id+"F0.wireOp",EDGE,"E7"),sQuery(id+"F0.wireOp",EDGE,"E8.MirrorC"),sQuery(id+"F0.wireOp",EDGE,"E9.MirrorC"),sQuery(id+"F0.wireOp",EDGE,"E10.MirrorC"),sQuery(id+"F0.wireOp",EDGE,"E11"),sQuery(id+"F0.wireOp",EDGE,"E14.MirrorC"),sQuery(id+"F0.wireOp",EDGE,"E15.MirrorC"),sQuery(id+"F0.wireOp",EDGE,"E17.MirrorC"),sQuery(id+"F0.wireOp",EDGE,"E19.bottom"),sQuery(id+"F0.wireOp",EDGE,"E20.left"),sQuery(id+"F0.wireOp",EDGE,"E21.bottom"),sQuery(id+"F0.wireOp",EDGE,"E22.left")])],"isStart":true})]});
            var Q10;
            Q10=makeQuery(id+"F7.boolean.opBoolean","COPY",EDGE,{"derivedFrom":makeQuery(id+"F7.opExtrude","CAP_EDGE",EDGE,{"disambiguationData":[OSD([sQuery(id+"F6.wireOp",EDGE,"E32.rect.left")])],"isStart":true})});
            var Q11;
            Q11=makeQuery(id+"F8.opFillet","BLEND_EDGE",EDGE,{"blendedFrom":[makeQuery(id+"F7.boolean.opBoolean","COPY",EDGE,{"derivedFrom":makeQuery(id+"F7.opExtrude","SWEPT_EDGE",EDGE,{"disambiguationData":[OSD([sQuery(id+"F6.wireOp",EDGE,"E32.rect.bottom"),sQuery(id+"F6.wireOp",EDGE,"E32.rect.left")])]})}),makeQuery(id+"F1.opExtrude","CAP_FACE",FACE,{"disambiguationData":[OSD([sQuery(id+"F0.wireOp",EDGE,"E7"),sQuery(id+"F0.wireOp",EDGE,"E8.MirrorC"),sQuery(id+"F0.wireOp",EDGE,"E9.MirrorC"),sQuery(id+"F0.wireOp",EDGE,"E10.MirrorC"),sQuery(id+"F0.wireOp",EDGE,"E11"),sQuery(id+"F0.wireOp",EDGE,"E14.MirrorC"),sQuery(id+"F0.wireOp",EDGE,"E15.MirrorC"),sQuery(id+"F0.wireOp",EDGE,"E17.MirrorC"),sQuery(id+"F0.wireOp",EDGE,"E19.bottom"),sQuery(id+"F0.wireOp",EDGE,"E20.left"),sQuery(id+"F0.wireOp",EDGE,"E21.bottom"),sQuery(id+"F0.wireOp",EDGE,"E22.left")])],"isStart":true})],"blendedInto":[makeQuery(id+"F1.opExtrude","CAP_FACE",FACE,{"disambiguationData":[OSD([sQuery(id+"F0.wireOp",EDGE,"E7"),sQuery(id+"F0.wireOp",EDGE,"E8.MirrorC"),sQuery(id+"F0.wireOp",EDGE,"E9.MirrorC"),sQuery(id+"F0.wireOp",EDGE,"E10.MirrorC"),sQuery(id+"F0.wireOp",EDGE,"E11"),sQuery(id+"F0.wireOp",EDGE,"E14.MirrorC"),sQuery(id+"F0.wireOp",EDGE,"E15.MirrorC"),sQuery(id+"F0.wireOp",EDGE,"E17.MirrorC"),sQuery(id+"F0.wireOp",EDGE,"E19.bottom"),sQuery(id+"F0.wireOp",EDGE,"E20.left"),sQuery(id+"F0.wireOp",EDGE,"E21.bottom"),sQuery(id+"F0.wireOp",EDGE,"E22.left")])],"isStart":true})]});
            var Q12;
            {var subQ0=sQuery(id+"F6.wireOp",EDGE,"E32.rect.bottom");Q12=makeQuery(id+"F7.boolean.opBoolean","COPY",EDGE,{"derivedFrom":makeQuery(id+"F7.opExtrude","CAP_EDGE",EDGE,{"disambiguationData":[OSD([subQ0]),TDD([makeQuery(id+"F6.imprint","IMPRINT",EDGE,{"disambiguationData":[TD([[makeQuery(id+"F6.imprint","INTERSECT",VERTEX,{"derivedFrom":[subQ0,sQuery(id+"F6.wireOp",EDGE,"E32.rect.left")]}),-1.0]])],"derivedFrom":subQ0})])],"isStart":true})});}
            var Q13;
            {var subQ0=sQuery(id+"F6.wireOp",EDGE,"E30.rect.left");Q13=makeQuery(id+"F7.boolean.opBoolean","COPY",EDGE,{"derivedFrom":makeQuery(id+"F7.opExtrude","CAP_EDGE",EDGE,{"disambiguationData":[OSD([subQ0]),TDD([makeQuery(id+"F6.imprint","IMPRINT",EDGE,{"disambiguationData":[TD([[makeQuery(id+"F6.imprint","INTERSECT",VERTEX,{"derivedFrom":[sQuery(id+"F6.wireOp",EDGE,"E30.rect.bottom"),subQ0]}),-1.0]])],"derivedFrom":subQ0})])],"isStart":true})});}
            var Q14;
            Q14=makeQuery(id+"F8.opFillet","BLEND_EDGE",EDGE,{"blendedFrom":[makeQuery(id+"F7.boolean.opBoolean","COPY",EDGE,{"derivedFrom":makeQuery(id+"F7.opExtrude","SWEPT_EDGE",EDGE,{"disambiguationData":[OSD([sQuery(id+"F6.wireOp",EDGE,"E30.rect.bottom"),sQuery(id+"F6.wireOp",EDGE,"E30.rect.left")])]})}),makeQuery(id+"F1.opExtrude","CAP_FACE",FACE,{"disambiguationData":[OSD([sQuery(id+"F0.wireOp",EDGE,"E7"),sQuery(id+"F0.wireOp",EDGE,"E8.MirrorC"),sQuery(id+"F0.wireOp",EDGE,"E9.MirrorC"),sQuery(id+"F0.wireOp",EDGE,"E10.MirrorC"),sQuery(id+"F0.wireOp",EDGE,"E11"),sQuery(id+"F0.wireOp",EDGE,"E14.MirrorC"),sQuery(id+"F0.wireOp",EDGE,"E15.MirrorC"),sQuery(id+"F0.wireOp",EDGE,"E17.MirrorC"),sQuery(id+"F0.wireOp",EDGE,"E19.bottom"),sQuery(id+"F0.wireOp",EDGE,"E20.left"),sQuery(id+"F0.wireOp",EDGE,"E21.bottom"),sQuery(id+"F0.wireOp",EDGE,"E22.left")])],"isStart":true})],"blendedInto":[makeQuery(id+"F1.opExtrude","CAP_FACE",FACE,{"disambiguationData":[OSD([sQuery(id+"F0.wireOp",EDGE,"E7"),sQuery(id+"F0.wireOp",EDGE,"E8.MirrorC"),sQuery(id+"F0.wireOp",EDGE,"E9.MirrorC"),sQuery(id+"F0.wireOp",EDGE,"E10.MirrorC"),sQuery(id+"F0.wireOp",EDGE,"E11"),sQuery(id+"F0.wireOp",EDGE,"E14.MirrorC"),sQuery(id+"F0.wireOp",EDGE,"E15.MirrorC"),sQuery(id+"F0.wireOp",EDGE,"E17.MirrorC"),sQuery(id+"F0.wireOp",EDGE,"E19.bottom"),sQuery(id+"F0.wireOp",EDGE,"E20.left"),sQuery(id+"F0.wireOp",EDGE,"E21.bottom"),sQuery(id+"F0.wireOp",EDGE,"E22.left")])],"isStart":true})]});
            var Q15;
            {var subQ0=sQuery(id+"F6.wireOp",EDGE,"E30.rect.bottom");Q15=makeQuery(id+"F7.boolean.opBoolean","COPY",EDGE,{"derivedFrom":makeQuery(id+"F7.opExtrude","CAP_EDGE",EDGE,{"disambiguationData":[OSD([subQ0]),TDD([makeQuery(id+"F6.imprint","IMPRINT",EDGE,{"disambiguationData":[TD([[makeQuery(id+"F6.imprint","INTERSECT",VERTEX,{"derivedFrom":[subQ0,sQuery(id+"F6.wireOp",EDGE,"E30.rect.left")]}),-1.0]])],"derivedFrom":subQ0})])],"isStart":true})});}
            var Q16;
            {var subQ0=sQuery(id+"F6.wireOp",EDGE,"E31.rect.right");Q16=makeQuery(id+"F7.boolean.opBoolean","COPY",EDGE,{"derivedFrom":makeQuery(id+"F7.opExtrude","CAP_EDGE",EDGE,{"disambiguationData":[OSD([subQ0]),TDD([makeQuery(id+"F6.imprint","IMPRINT",EDGE,{"disambiguationData":[TD([[makeQuery(id+"F6.imprint","INTERSECT",VERTEX,{"derivedFrom":[sQuery(id+"F6.wireOp",EDGE,"E31.rect.top"),subQ0]}),1.0]])],"derivedFrom":subQ0})])],"isStart":true})});}
            var Q17;
            Q17=makeQuery(id+"F8.opFillet","BLEND_EDGE",EDGE,{"blendedFrom":[makeQuery(id+"F7.boolean.opBoolean","COPY",EDGE,{"derivedFrom":makeQuery(id+"F7.opExtrude","SWEPT_EDGE",EDGE,{"disambiguationData":[OSD([sQuery(id+"F6.wireOp",EDGE,"E31.rect.top"),sQuery(id+"F6.wireOp",EDGE,"E31.rect.right")])]})}),makeQuery(id+"F1.opExtrude","CAP_FACE",FACE,{"disambiguationData":[OSD([sQuery(id+"F0.wireOp",EDGE,"E7"),sQuery(id+"F0.wireOp",EDGE,"E8.MirrorC"),sQuery(id+"F0.wireOp",EDGE,"E9.MirrorC"),sQuery(id+"F0.wireOp",EDGE,"E10.MirrorC"),sQuery(id+"F0.wireOp",EDGE,"E11"),sQuery(id+"F0.wireOp",EDGE,"E14.MirrorC"),sQuery(id+"F0.wireOp",EDGE,"E15.MirrorC"),sQuery(id+"F0.wireOp",EDGE,"E17.MirrorC"),sQuery(id+"F0.wireOp",EDGE,"E19.bottom"),sQuery(id+"F0.wireOp",EDGE,"E20.left"),sQuery(id+"F0.wireOp",EDGE,"E21.bottom"),sQuery(id+"F0.wireOp",EDGE,"E22.left")])],"isStart":true})],"blendedInto":[makeQuery(id+"F1.opExtrude","CAP_FACE",FACE,{"disambiguationData":[OSD([sQuery(id+"F0.wireOp",EDGE,"E7"),sQuery(id+"F0.wireOp",EDGE,"E8.MirrorC"),sQuery(id+"F0.wireOp",EDGE,"E9.MirrorC"),sQuery(id+"F0.wireOp",EDGE,"E10.MirrorC"),sQuery(id+"F0.wireOp",EDGE,"E11"),sQuery(id+"F0.wireOp",EDGE,"E14.MirrorC"),sQuery(id+"F0.wireOp",EDGE,"E15.MirrorC"),sQuery(id+"F0.wireOp",EDGE,"E17.MirrorC"),sQuery(id+"F0.wireOp",EDGE,"E19.bottom"),sQuery(id+"F0.wireOp",EDGE,"E20.left"),sQuery(id+"F0.wireOp",EDGE,"E21.bottom"),sQuery(id+"F0.wireOp",EDGE,"E22.left")])],"isStart":true})]});
            var Q18;
            Q18=makeQuery(id+"F7.boolean.opBoolean","COPY",EDGE,{"derivedFrom":makeQuery(id+"F7.opExtrude","CAP_EDGE",EDGE,{"disambiguationData":[OSD([sQuery(id+"F6.wireOp",EDGE,"E31.rect.top")])],"isStart":true})});
            var Q19;
            Q19=makeQuery(id+"F8.opFillet","BLEND_EDGE",EDGE,{"blendedFrom":[makeQuery(id+"F7.boolean.opBoolean","COPY",EDGE,{"derivedFrom":makeQuery(id+"F7.opExtrude","SWEPT_EDGE",EDGE,{"disambiguationData":[OSD([sQuery(id+"F6.wireOp",EDGE,"E31.rect.top"),sQuery(id+"F6.wireOp",EDGE,"E31.rect.left")])]})}),makeQuery(id+"F1.opExtrude","CAP_FACE",FACE,{"disambiguationData":[OSD([sQuery(id+"F0.wireOp",EDGE,"E7"),sQuery(id+"F0.wireOp",EDGE,"E8.MirrorC"),sQuery(id+"F0.wireOp",EDGE,"E9.MirrorC"),sQuery(id+"F0.wireOp",EDGE,"E10.MirrorC"),sQuery(id+"F0.wireOp",EDGE,"E11"),sQuery(id+"F0.wireOp",EDGE,"E14.MirrorC"),sQuery(id+"F0.wireOp",EDGE,"E15.MirrorC"),sQuery(id+"F0.wireOp",EDGE,"E17.MirrorC"),sQuery(id+"F0.wireOp",EDGE,"E19.bottom"),sQuery(id+"F0.wireOp",EDGE,"E20.left"),sQuery(id+"F0.wireOp",EDGE,"E21.bottom"),sQuery(id+"F0.wireOp",EDGE,"E22.left")])],"isStart":true})],"blendedInto":[makeQuery(id+"F1.opExtrude","CAP_FACE",FACE,{"disambiguationData":[OSD([sQuery(id+"F0.wireOp",EDGE,"E7"),sQuery(id+"F0.wireOp",EDGE,"E8.MirrorC"),sQuery(id+"F0.wireOp",EDGE,"E9.MirrorC"),sQuery(id+"F0.wireOp",EDGE,"E10.MirrorC"),sQuery(id+"F0.wireOp",EDGE,"E11"),sQuery(id+"F0.wireOp",EDGE,"E14.MirrorC"),sQuery(id+"F0.wireOp",EDGE,"E15.MirrorC"),sQuery(id+"F0.wireOp",EDGE,"E17.MirrorC"),sQuery(id+"F0.wireOp",EDGE,"E19.bottom"),sQuery(id+"F0.wireOp",EDGE,"E20.left"),sQuery(id+"F0.wireOp",EDGE,"E21.bottom"),sQuery(id+"F0.wireOp",EDGE,"E22.left")])],"isStart":true})]});
            var Q20;
            {var subQ0=sQuery(id+"F6.wireOp",EDGE,"E31.rect.left");Q20=makeQuery(id+"F7.boolean.opBoolean","COPY",EDGE,{"derivedFrom":makeQuery(id+"F7.opExtrude","CAP_EDGE",EDGE,{"disambiguationData":[OSD([subQ0]),TDD([makeQuery(id+"F6.imprint","IMPRINT",EDGE,{"disambiguationData":[TD([[makeQuery(id+"F6.imprint","INTERSECT",VERTEX,{"derivedFrom":[sQuery(id+"F6.wireOp",EDGE,"E31.rect.top"),subQ0]}),1.0]])],"derivedFrom":subQ0})])],"isStart":true})});}
            var Q21;
            {var subQ0=sQuery(id+"F6.wireOp",EDGE,"E30.rect.top");Q21=makeQuery(id+"F7.boolean.opBoolean","COPY",EDGE,{"derivedFrom":makeQuery(id+"F7.opExtrude","CAP_EDGE",EDGE,{"disambiguationData":[OSD([subQ0]),TDD([makeQuery(id+"F6.imprint","IMPRINT",EDGE,{"disambiguationData":[TD([[makeQuery(id+"F6.imprint","INTERSECT",VERTEX,{"derivedFrom":[subQ0,sQuery(id+"F6.wireOp",EDGE,"E30.rect.right")]}),1.0]])],"derivedFrom":subQ0})])],"isStart":true})});}
            var Q22;
            Q22=makeQuery(id+"F7.boolean.opBoolean","COPY",EDGE,{"derivedFrom":makeQuery(id+"F7.opExtrude","CAP_EDGE",EDGE,{"disambiguationData":[OSD([sQuery(id+"F6.wireOp",EDGE,"E32.rect.right")])],"isStart":true})});
            var Q23;
            Q23=makeQuery(id+"F8.opFillet","BLEND_EDGE",EDGE,{"blendedFrom":[makeQuery(id+"F7.boolean.opBoolean","COPY",EDGE,{"derivedFrom":makeQuery(id+"F7.opExtrude","SWEPT_EDGE",EDGE,{"disambiguationData":[OSD([sQuery(id+"F6.wireOp",EDGE,"E32.rect.top"),sQuery(id+"F6.wireOp",EDGE,"E32.rect.right")])]})}),makeQuery(id+"F1.opExtrude","CAP_FACE",FACE,{"disambiguationData":[OSD([sQuery(id+"F0.wireOp",EDGE,"E7"),sQuery(id+"F0.wireOp",EDGE,"E8.MirrorC"),sQuery(id+"F0.wireOp",EDGE,"E9.MirrorC"),sQuery(id+"F0.wireOp",EDGE,"E10.MirrorC"),sQuery(id+"F0.wireOp",EDGE,"E11"),sQuery(id+"F0.wireOp",EDGE,"E14.MirrorC"),sQuery(id+"F0.wireOp",EDGE,"E15.MirrorC"),sQuery(id+"F0.wireOp",EDGE,"E17.MirrorC"),sQuery(id+"F0.wireOp",EDGE,"E19.bottom"),sQuery(id+"F0.wireOp",EDGE,"E20.left"),sQuery(id+"F0.wireOp",EDGE,"E21.bottom"),sQuery(id+"F0.wireOp",EDGE,"E22.left")])],"isStart":true})],"blendedInto":[makeQuery(id+"F1.opExtrude","CAP_FACE",FACE,{"disambiguationData":[OSD([sQuery(id+"F0.wireOp",EDGE,"E7"),sQuery(id+"F0.wireOp",EDGE,"E8.MirrorC"),sQuery(id+"F0.wireOp",EDGE,"E9.MirrorC"),sQuery(id+"F0.wireOp",EDGE,"E10.MirrorC"),sQuery(id+"F0.wireOp",EDGE,"E11"),sQuery(id+"F0.wireOp",EDGE,"E14.MirrorC"),sQuery(id+"F0.wireOp",EDGE,"E15.MirrorC"),sQuery(id+"F0.wireOp",EDGE,"E17.MirrorC"),sQuery(id+"F0.wireOp",EDGE,"E19.bottom"),sQuery(id+"F0.wireOp",EDGE,"E20.left"),sQuery(id+"F0.wireOp",EDGE,"E21.bottom"),sQuery(id+"F0.wireOp",EDGE,"E22.left")])],"isStart":true})]});
            var Q24;
            Q24=makeQuery(id+"F8.opFillet","BLEND_EDGE",EDGE,{"blendedFrom":[makeQuery(id+"F7.boolean.opBoolean","COPY",EDGE,{"derivedFrom":makeQuery(id+"F7.opExtrude","SWEPT_EDGE",EDGE,{"disambiguationData":[OSD([sQuery(id+"F6.wireOp",EDGE,"E32.rect.bottom"),sQuery(id+"F6.wireOp",EDGE,"E32.rect.right")])]})}),makeQuery(id+"F1.opExtrude","CAP_FACE",FACE,{"disambiguationData":[OSD([sQuery(id+"F0.wireOp",EDGE,"E7"),sQuery(id+"F0.wireOp",EDGE,"E8.MirrorC"),sQuery(id+"F0.wireOp",EDGE,"E9.MirrorC"),sQuery(id+"F0.wireOp",EDGE,"E10.MirrorC"),sQuery(id+"F0.wireOp",EDGE,"E11"),sQuery(id+"F0.wireOp",EDGE,"E14.MirrorC"),sQuery(id+"F0.wireOp",EDGE,"E15.MirrorC"),sQuery(id+"F0.wireOp",EDGE,"E17.MirrorC"),sQuery(id+"F0.wireOp",EDGE,"E19.bottom"),sQuery(id+"F0.wireOp",EDGE,"E20.left"),sQuery(id+"F0.wireOp",EDGE,"E21.bottom"),sQuery(id+"F0.wireOp",EDGE,"E22.left")])],"isStart":true})],"blendedInto":[makeQuery(id+"F1.opExtrude","CAP_FACE",FACE,{"disambiguationData":[OSD([sQuery(id+"F0.wireOp",EDGE,"E7"),sQuery(id+"F0.wireOp",EDGE,"E8.MirrorC"),sQuery(id+"F0.wireOp",EDGE,"E9.MirrorC"),sQuery(id+"F0.wireOp",EDGE,"E10.MirrorC"),sQuery(id+"F0.wireOp",EDGE,"E11"),sQuery(id+"F0.wireOp",EDGE,"E14.MirrorC"),sQuery(id+"F0.wireOp",EDGE,"E15.MirrorC"),sQuery(id+"F0.wireOp",EDGE,"E17.MirrorC"),sQuery(id+"F0.wireOp",EDGE,"E19.bottom"),sQuery(id+"F0.wireOp",EDGE,"E20.left"),sQuery(id+"F0.wireOp",EDGE,"E21.bottom"),sQuery(id+"F0.wireOp",EDGE,"E22.left")])],"isStart":true})]});
            var Q25;
            {var subQ0=sQuery(id+"F6.wireOp",EDGE,"E32.rect.bottom");Q25=makeQuery(id+"F7.boolean.opBoolean","COPY",EDGE,{"derivedFrom":makeQuery(id+"F7.opExtrude","CAP_EDGE",EDGE,{"disambiguationData":[OSD([subQ0]),TDD([makeQuery(id+"F6.imprint","IMPRINT",EDGE,{"disambiguationData":[TD([[makeQuery(id+"F6.imprint","INTERSECT",VERTEX,{"derivedFrom":[subQ0,sQuery(id+"F6.wireOp",EDGE,"E32.rect.right")]}),1.0]])],"derivedFrom":subQ0})])],"isStart":true})});}
            var Q26;
            {var subQ0=sQuery(id+"F6.wireOp",EDGE,"E32.rect.top");Q26=makeQuery(id+"F7.boolean.opBoolean","COPY",EDGE,{"derivedFrom":makeQuery(id+"F7.opExtrude","CAP_EDGE",EDGE,{"disambiguationData":[OSD([subQ0]),TDD([makeQuery(id+"F6.imprint","IMPRINT",EDGE,{"disambiguationData":[TD([[makeQuery(id+"F6.imprint","INTERSECT",VERTEX,{"derivedFrom":[subQ0,sQuery(id+"F6.wireOp",EDGE,"E32.rect.right")]}),1.0]])],"derivedFrom":subQ0})])],"isStart":true})});}
            var Q27;
            {var subQ0=sQuery(id+"F6.wireOp",EDGE,"E30.rect.right");Q27=makeQuery(id+"F7.boolean.opBoolean","COPY",EDGE,{"derivedFrom":makeQuery(id+"F7.opExtrude","CAP_EDGE",EDGE,{"disambiguationData":[OSD([subQ0]),TDD([makeQuery(id+"F6.imprint","IMPRINT",EDGE,{"disambiguationData":[TD([[makeQuery(id+"F6.imprint","INTERSECT",VERTEX,{"derivedFrom":[sQuery(id+"F6.wireOp",EDGE,"E30.rect.top"),subQ0]}),1.0]])],"derivedFrom":subQ0})])],"isStart":true})});}
            var Q28;
            Q28=makeQuery(id+"F8.opFillet","BLEND_EDGE",EDGE,{"blendedFrom":[makeQuery(id+"F7.boolean.opBoolean","COPY",EDGE,{"derivedFrom":makeQuery(id+"F7.opExtrude","SWEPT_EDGE",EDGE,{"disambiguationData":[OSD([sQuery(id+"F6.wireOp",EDGE,"E30.rect.top"),sQuery(id+"F6.wireOp",EDGE,"E30.rect.right")])]})}),makeQuery(id+"F1.opExtrude","CAP_FACE",FACE,{"disambiguationData":[OSD([sQuery(id+"F0.wireOp",EDGE,"E7"),sQuery(id+"F0.wireOp",EDGE,"E8.MirrorC"),sQuery(id+"F0.wireOp",EDGE,"E9.MirrorC"),sQuery(id+"F0.wireOp",EDGE,"E10.MirrorC"),sQuery(id+"F0.wireOp",EDGE,"E11"),sQuery(id+"F0.wireOp",EDGE,"E14.MirrorC"),sQuery(id+"F0.wireOp",EDGE,"E15.MirrorC"),sQuery(id+"F0.wireOp",EDGE,"E17.MirrorC"),sQuery(id+"F0.wireOp",EDGE,"E19.bottom"),sQuery(id+"F0.wireOp",EDGE,"E20.left"),sQuery(id+"F0.wireOp",EDGE,"E21.bottom"),sQuery(id+"F0.wireOp",EDGE,"E22.left")])],"isStart":true})],"blendedInto":[makeQuery(id+"F1.opExtrude","CAP_FACE",FACE,{"disambiguationData":[OSD([sQuery(id+"F0.wireOp",EDGE,"E7"),sQuery(id+"F0.wireOp",EDGE,"E8.MirrorC"),sQuery(id+"F0.wireOp",EDGE,"E9.MirrorC"),sQuery(id+"F0.wireOp",EDGE,"E10.MirrorC"),sQuery(id+"F0.wireOp",EDGE,"E11"),sQuery(id+"F0.wireOp",EDGE,"E14.MirrorC"),sQuery(id+"F0.wireOp",EDGE,"E15.MirrorC"),sQuery(id+"F0.wireOp",EDGE,"E17.MirrorC"),sQuery(id+"F0.wireOp",EDGE,"E19.bottom"),sQuery(id+"F0.wireOp",EDGE,"E20.left"),sQuery(id+"F0.wireOp",EDGE,"E21.bottom"),sQuery(id+"F0.wireOp",EDGE,"E22.left")])],"isStart":true})]});
            var Q29;
            {var subQ0=sQuery(id+"F6.wireOp",EDGE,"E30.rect.right");Q29=makeQuery(id+"F7.boolean.opBoolean","COPY",EDGE,{"derivedFrom":makeQuery(id+"F7.opExtrude","CAP_EDGE",EDGE,{"disambiguationData":[OSD([subQ0]),TDD([makeQuery(id+"F6.imprint","IMPRINT",EDGE,{"disambiguationData":[TD([[makeQuery(id+"F6.imprint","INTERSECT",VERTEX,{"derivedFrom":[sQuery(id+"F6.wireOp",EDGE,"E30.rect.bottom"),subQ0]}),-1.0]])],"derivedFrom":subQ0})])],"isStart":true})});}
            var Q30;
            Q30=makeQuery(id+"F8.opFillet","BLEND_EDGE",EDGE,{"blendedFrom":[makeQuery(id+"F7.boolean.opBoolean","COPY",EDGE,{"derivedFrom":makeQuery(id+"F7.opExtrude","SWEPT_EDGE",EDGE,{"disambiguationData":[OSD([sQuery(id+"F6.wireOp",EDGE,"E30.rect.bottom"),sQuery(id+"F6.wireOp",EDGE,"E30.rect.right")])]})}),makeQuery(id+"F1.opExtrude","CAP_FACE",FACE,{"disambiguationData":[OSD([sQuery(id+"F0.wireOp",EDGE,"E7"),sQuery(id+"F0.wireOp",EDGE,"E8.MirrorC"),sQuery(id+"F0.wireOp",EDGE,"E9.MirrorC"),sQuery(id+"F0.wireOp",EDGE,"E10.MirrorC"),sQuery(id+"F0.wireOp",EDGE,"E11"),sQuery(id+"F0.wireOp",EDGE,"E14.MirrorC"),sQuery(id+"F0.wireOp",EDGE,"E15.MirrorC"),sQuery(id+"F0.wireOp",EDGE,"E17.MirrorC"),sQuery(id+"F0.wireOp",EDGE,"E19.bottom"),sQuery(id+"F0.wireOp",EDGE,"E20.left"),sQuery(id+"F0.wireOp",EDGE,"E21.bottom"),sQuery(id+"F0.wireOp",EDGE,"E22.left")])],"isStart":true})],"blendedInto":[makeQuery(id+"F1.opExtrude","CAP_FACE",FACE,{"disambiguationData":[OSD([sQuery(id+"F0.wireOp",EDGE,"E7"),sQuery(id+"F0.wireOp",EDGE,"E8.MirrorC"),sQuery(id+"F0.wireOp",EDGE,"E9.MirrorC"),sQuery(id+"F0.wireOp",EDGE,"E10.MirrorC"),sQuery(id+"F0.wireOp",EDGE,"E11"),sQuery(id+"F0.wireOp",EDGE,"E14.MirrorC"),sQuery(id+"F0.wireOp",EDGE,"E15.MirrorC"),sQuery(id+"F0.wireOp",EDGE,"E17.MirrorC"),sQuery(id+"F0.wireOp",EDGE,"E19.bottom"),sQuery(id+"F0.wireOp",EDGE,"E20.left"),sQuery(id+"F0.wireOp",EDGE,"E21.bottom"),sQuery(id+"F0.wireOp",EDGE,"E22.left")])],"isStart":true})]});
            var Q31;
            {var subQ0=sQuery(id+"F6.wireOp",EDGE,"E30.rect.bottom");Q31=makeQuery(id+"F7.boolean.opBoolean","COPY",EDGE,{"derivedFrom":makeQuery(id+"F7.opExtrude","CAP_EDGE",EDGE,{"disambiguationData":[OSD([subQ0]),TDD([makeQuery(id+"F6.imprint","IMPRINT",EDGE,{"disambiguationData":[TD([[makeQuery(id+"F6.imprint","INTERSECT",VERTEX,{"derivedFrom":[subQ0,sQuery(id+"F6.wireOp",EDGE,"E30.rect.right")]}),1.0]])],"derivedFrom":subQ0})])],"isStart":true})});}
            var Q32;
            Q32=makeQuery(id+"F7.boolean.opBoolean","INTERSECT",EDGE,{"derivedFrom":[makeQuery(id+"F1.opExtrude","CAP_FACE",FACE,{"disambiguationData":[OSD([sQuery(id+"F0.wireOp",EDGE,"E7"),sQuery(id+"F0.wireOp",EDGE,"E8.MirrorC"),sQuery(id+"F0.wireOp",EDGE,"E9.MirrorC"),sQuery(id+"F0.wireOp",EDGE,"E10.MirrorC"),sQuery(id+"F0.wireOp",EDGE,"E11"),sQuery(id+"F0.wireOp",EDGE,"E14.MirrorC"),sQuery(id+"F0.wireOp",EDGE,"E15.MirrorC"),sQuery(id+"F0.wireOp",EDGE,"E17.MirrorC"),sQuery(id+"F0.wireOp",EDGE,"E19.bottom"),sQuery(id+"F0.wireOp",EDGE,"E20.left"),sQuery(id+"F0.wireOp",EDGE,"E21.bottom"),sQuery(id+"F0.wireOp",EDGE,"E22.left")])],"isStart":false}),makeQuery(id+"F7.opExtrude","SWEPT_FACE",FACE,{"disambiguationData":[OSD([sQuery(id+"F6.wireOp",EDGE,"E31.rect.bottom")])]})]});
            var Q33;
            Q33=makeQuery(id+"F8.opFillet","BLEND_EDGE",EDGE,{"blendedFrom":[makeQuery(id+"F7.boolean.opBoolean","COPY",EDGE,{"derivedFrom":makeQuery(id+"F7.opExtrude","SWEPT_EDGE",EDGE,{"disambiguationData":[OSD([sQuery(id+"F6.wireOp",EDGE,"E31.rect.bottom"),sQuery(id+"F6.wireOp",EDGE,"E31.rect.right")])]})}),makeQuery(id+"F1.opExtrude","CAP_FACE",FACE,{"disambiguationData":[OSD([sQuery(id+"F0.wireOp",EDGE,"E7"),sQuery(id+"F0.wireOp",EDGE,"E8.MirrorC"),sQuery(id+"F0.wireOp",EDGE,"E9.MirrorC"),sQuery(id+"F0.wireOp",EDGE,"E10.MirrorC"),sQuery(id+"F0.wireOp",EDGE,"E11"),sQuery(id+"F0.wireOp",EDGE,"E14.MirrorC"),sQuery(id+"F0.wireOp",EDGE,"E15.MirrorC"),sQuery(id+"F0.wireOp",EDGE,"E17.MirrorC"),sQuery(id+"F0.wireOp",EDGE,"E19.bottom"),sQuery(id+"F0.wireOp",EDGE,"E20.left"),sQuery(id+"F0.wireOp",EDGE,"E21.bottom"),sQuery(id+"F0.wireOp",EDGE,"E22.left")])],"isStart":false})],"blendedInto":[makeQuery(id+"F1.opExtrude","CAP_FACE",FACE,{"disambiguationData":[OSD([sQuery(id+"F0.wireOp",EDGE,"E7"),sQuery(id+"F0.wireOp",EDGE,"E8.MirrorC"),sQuery(id+"F0.wireOp",EDGE,"E9.MirrorC"),sQuery(id+"F0.wireOp",EDGE,"E10.MirrorC"),sQuery(id+"F0.wireOp",EDGE,"E11"),sQuery(id+"F0.wireOp",EDGE,"E14.MirrorC"),sQuery(id+"F0.wireOp",EDGE,"E15.MirrorC"),sQuery(id+"F0.wireOp",EDGE,"E17.MirrorC"),sQuery(id+"F0.wireOp",EDGE,"E19.bottom"),sQuery(id+"F0.wireOp",EDGE,"E20.left"),sQuery(id+"F0.wireOp",EDGE,"E21.bottom"),sQuery(id+"F0.wireOp",EDGE,"E22.left")])],"isStart":false})]});
            var Q34;
            {var subQ0=sQuery(id+"F6.wireOp",EDGE,"E31.rect.right");Q34=makeQuery(id+"F7.boolean.opBoolean","INTERSECT",EDGE,{"derivedFrom":[makeQuery(id+"F1.opExtrude","CAP_FACE",FACE,{"disambiguationData":[OSD([sQuery(id+"F0.wireOp",EDGE,"E7"),sQuery(id+"F0.wireOp",EDGE,"E8.MirrorC"),sQuery(id+"F0.wireOp",EDGE,"E9.MirrorC"),sQuery(id+"F0.wireOp",EDGE,"E10.MirrorC"),sQuery(id+"F0.wireOp",EDGE,"E11"),sQuery(id+"F0.wireOp",EDGE,"E14.MirrorC"),sQuery(id+"F0.wireOp",EDGE,"E15.MirrorC"),sQuery(id+"F0.wireOp",EDGE,"E17.MirrorC"),sQuery(id+"F0.wireOp",EDGE,"E19.bottom"),sQuery(id+"F0.wireOp",EDGE,"E20.left"),sQuery(id+"F0.wireOp",EDGE,"E21.bottom"),sQuery(id+"F0.wireOp",EDGE,"E22.left")])],"isStart":false}),makeQuery(id+"F7.opExtrude","SWEPT_FACE",FACE,{"disambiguationData":[OSD([subQ0]),TDD([makeQuery(id+"F6.imprint","IMPRINT",EDGE,{"disambiguationData":[TD([[makeQuery(id+"F6.imprint","INTERSECT",VERTEX,{"derivedFrom":[sQuery(id+"F6.wireOp",EDGE,"E31.rect.bottom"),subQ0]}),-1.0]])],"derivedFrom":subQ0})])]})]});}
            var Q35;
            {var subQ0=sQuery(id+"F6.wireOp",EDGE,"E30.rect.top");Q35=makeQuery(id+"F7.boolean.opBoolean","INTERSECT",EDGE,{"derivedFrom":[makeQuery(id+"F1.opExtrude","CAP_FACE",FACE,{"disambiguationData":[OSD([sQuery(id+"F0.wireOp",EDGE,"E7"),sQuery(id+"F0.wireOp",EDGE,"E8.MirrorC"),sQuery(id+"F0.wireOp",EDGE,"E9.MirrorC"),sQuery(id+"F0.wireOp",EDGE,"E10.MirrorC"),sQuery(id+"F0.wireOp",EDGE,"E11"),sQuery(id+"F0.wireOp",EDGE,"E14.MirrorC"),sQuery(id+"F0.wireOp",EDGE,"E15.MirrorC"),sQuery(id+"F0.wireOp",EDGE,"E17.MirrorC"),sQuery(id+"F0.wireOp",EDGE,"E19.bottom"),sQuery(id+"F0.wireOp",EDGE,"E20.left"),sQuery(id+"F0.wireOp",EDGE,"E21.bottom"),sQuery(id+"F0.wireOp",EDGE,"E22.left")])],"isStart":false}),makeQuery(id+"F7.opExtrude","SWEPT_FACE",FACE,{"disambiguationData":[OSD([subQ0]),TDD([makeQuery(id+"F6.imprint","IMPRINT",EDGE,{"disambiguationData":[TD([[makeQuery(id+"F6.imprint","INTERSECT",VERTEX,{"derivedFrom":[subQ0,sQuery(id+"F6.wireOp",EDGE,"E30.rect.left")]}),-1.0]])],"derivedFrom":subQ0})])]})]});}
            var Q36;
            Q36=makeQuery(id+"F8.opFillet","BLEND_EDGE",EDGE,{"blendedFrom":[makeQuery(id+"F7.boolean.opBoolean","COPY",EDGE,{"derivedFrom":makeQuery(id+"F7.opExtrude","SWEPT_EDGE",EDGE,{"disambiguationData":[OSD([sQuery(id+"F6.wireOp",EDGE,"E30.rect.top"),sQuery(id+"F6.wireOp",EDGE,"E30.rect.left")])]})}),makeQuery(id+"F1.opExtrude","CAP_FACE",FACE,{"disambiguationData":[OSD([sQuery(id+"F0.wireOp",EDGE,"E7"),sQuery(id+"F0.wireOp",EDGE,"E8.MirrorC"),sQuery(id+"F0.wireOp",EDGE,"E9.MirrorC"),sQuery(id+"F0.wireOp",EDGE,"E10.MirrorC"),sQuery(id+"F0.wireOp",EDGE,"E11"),sQuery(id+"F0.wireOp",EDGE,"E14.MirrorC"),sQuery(id+"F0.wireOp",EDGE,"E15.MirrorC"),sQuery(id+"F0.wireOp",EDGE,"E17.MirrorC"),sQuery(id+"F0.wireOp",EDGE,"E19.bottom"),sQuery(id+"F0.wireOp",EDGE,"E20.left"),sQuery(id+"F0.wireOp",EDGE,"E21.bottom"),sQuery(id+"F0.wireOp",EDGE,"E22.left")])],"isStart":false})],"blendedInto":[makeQuery(id+"F1.opExtrude","CAP_FACE",FACE,{"disambiguationData":[OSD([sQuery(id+"F0.wireOp",EDGE,"E7"),sQuery(id+"F0.wireOp",EDGE,"E8.MirrorC"),sQuery(id+"F0.wireOp",EDGE,"E9.MirrorC"),sQuery(id+"F0.wireOp",EDGE,"E10.MirrorC"),sQuery(id+"F0.wireOp",EDGE,"E11"),sQuery(id+"F0.wireOp",EDGE,"E14.MirrorC"),sQuery(id+"F0.wireOp",EDGE,"E15.MirrorC"),sQuery(id+"F0.wireOp",EDGE,"E17.MirrorC"),sQuery(id+"F0.wireOp",EDGE,"E19.bottom"),sQuery(id+"F0.wireOp",EDGE,"E20.left"),sQuery(id+"F0.wireOp",EDGE,"E21.bottom"),sQuery(id+"F0.wireOp",EDGE,"E22.left")])],"isStart":false})]});
            var Q37;
            {var subQ0=sQuery(id+"F6.wireOp",EDGE,"E30.rect.left");Q37=makeQuery(id+"F7.boolean.opBoolean","INTERSECT",EDGE,{"derivedFrom":[makeQuery(id+"F1.opExtrude","CAP_FACE",FACE,{"disambiguationData":[OSD([sQuery(id+"F0.wireOp",EDGE,"E7"),sQuery(id+"F0.wireOp",EDGE,"E8.MirrorC"),sQuery(id+"F0.wireOp",EDGE,"E9.MirrorC"),sQuery(id+"F0.wireOp",EDGE,"E10.MirrorC"),sQuery(id+"F0.wireOp",EDGE,"E11"),sQuery(id+"F0.wireOp",EDGE,"E14.MirrorC"),sQuery(id+"F0.wireOp",EDGE,"E15.MirrorC"),sQuery(id+"F0.wireOp",EDGE,"E17.MirrorC"),sQuery(id+"F0.wireOp",EDGE,"E19.bottom"),sQuery(id+"F0.wireOp",EDGE,"E20.left"),sQuery(id+"F0.wireOp",EDGE,"E21.bottom"),sQuery(id+"F0.wireOp",EDGE,"E22.left")])],"isStart":false}),makeQuery(id+"F7.opExtrude","SWEPT_FACE",FACE,{"disambiguationData":[OSD([subQ0]),TDD([makeQuery(id+"F6.imprint","IMPRINT",EDGE,{"disambiguationData":[TD([[makeQuery(id+"F6.imprint","INTERSECT",VERTEX,{"derivedFrom":[sQuery(id+"F6.wireOp",EDGE,"E30.rect.top"),subQ0]}),1.0]])],"derivedFrom":subQ0})])]})]});}
            var Q38;
            {var subQ0=sQuery(id+"F6.wireOp",EDGE,"E32.rect.top");Q38=makeQuery(id+"F7.boolean.opBoolean","INTERSECT",EDGE,{"derivedFrom":[makeQuery(id+"F1.opExtrude","CAP_FACE",FACE,{"disambiguationData":[OSD([sQuery(id+"F0.wireOp",EDGE,"E7"),sQuery(id+"F0.wireOp",EDGE,"E8.MirrorC"),sQuery(id+"F0.wireOp",EDGE,"E9.MirrorC"),sQuery(id+"F0.wireOp",EDGE,"E10.MirrorC"),sQuery(id+"F0.wireOp",EDGE,"E11"),sQuery(id+"F0.wireOp",EDGE,"E14.MirrorC"),sQuery(id+"F0.wireOp",EDGE,"E15.MirrorC"),sQuery(id+"F0.wireOp",EDGE,"E17.MirrorC"),sQuery(id+"F0.wireOp",EDGE,"E19.bottom"),sQuery(id+"F0.wireOp",EDGE,"E20.left"),sQuery(id+"F0.wireOp",EDGE,"E21.bottom"),sQuery(id+"F0.wireOp",EDGE,"E22.left")])],"isStart":false}),makeQuery(id+"F7.opExtrude","SWEPT_FACE",FACE,{"disambiguationData":[OSD([subQ0]),TDD([makeQuery(id+"F6.imprint","IMPRINT",EDGE,{"disambiguationData":[TD([[makeQuery(id+"F6.imprint","INTERSECT",VERTEX,{"derivedFrom":[subQ0,sQuery(id+"F6.wireOp",EDGE,"E32.rect.left")]}),-1.0]])],"derivedFrom":subQ0})])]})]});}
            var Q39;
            Q39=makeQuery(id+"F8.opFillet","BLEND_EDGE",EDGE,{"blendedFrom":[makeQuery(id+"F7.boolean.opBoolean","COPY",EDGE,{"derivedFrom":makeQuery(id+"F7.opExtrude","SWEPT_EDGE",EDGE,{"disambiguationData":[OSD([sQuery(id+"F6.wireOp",EDGE,"E32.rect.top"),sQuery(id+"F6.wireOp",EDGE,"E32.rect.left")])]})}),makeQuery(id+"F1.opExtrude","CAP_FACE",FACE,{"disambiguationData":[OSD([sQuery(id+"F0.wireOp",EDGE,"E7"),sQuery(id+"F0.wireOp",EDGE,"E8.MirrorC"),sQuery(id+"F0.wireOp",EDGE,"E9.MirrorC"),sQuery(id+"F0.wireOp",EDGE,"E10.MirrorC"),sQuery(id+"F0.wireOp",EDGE,"E11"),sQuery(id+"F0.wireOp",EDGE,"E14.MirrorC"),sQuery(id+"F0.wireOp",EDGE,"E15.MirrorC"),sQuery(id+"F0.wireOp",EDGE,"E17.MirrorC"),sQuery(id+"F0.wireOp",EDGE,"E19.bottom"),sQuery(id+"F0.wireOp",EDGE,"E20.left"),sQuery(id+"F0.wireOp",EDGE,"E21.bottom"),sQuery(id+"F0.wireOp",EDGE,"E22.left")])],"isStart":false})],"blendedInto":[makeQuery(id+"F1.opExtrude","CAP_FACE",FACE,{"disambiguationData":[OSD([sQuery(id+"F0.wireOp",EDGE,"E7"),sQuery(id+"F0.wireOp",EDGE,"E8.MirrorC"),sQuery(id+"F0.wireOp",EDGE,"E9.MirrorC"),sQuery(id+"F0.wireOp",EDGE,"E10.MirrorC"),sQuery(id+"F0.wireOp",EDGE,"E11"),sQuery(id+"F0.wireOp",EDGE,"E14.MirrorC"),sQuery(id+"F0.wireOp",EDGE,"E15.MirrorC"),sQuery(id+"F0.wireOp",EDGE,"E17.MirrorC"),sQuery(id+"F0.wireOp",EDGE,"E19.bottom"),sQuery(id+"F0.wireOp",EDGE,"E20.left"),sQuery(id+"F0.wireOp",EDGE,"E21.bottom"),sQuery(id+"F0.wireOp",EDGE,"E22.left")])],"isStart":false})]});
            var Q40;
            Q40=makeQuery(id+"F7.boolean.opBoolean","INTERSECT",EDGE,{"derivedFrom":[makeQuery(id+"F1.opExtrude","CAP_FACE",FACE,{"disambiguationData":[OSD([sQuery(id+"F0.wireOp",EDGE,"E7"),sQuery(id+"F0.wireOp",EDGE,"E8.MirrorC"),sQuery(id+"F0.wireOp",EDGE,"E9.MirrorC"),sQuery(id+"F0.wireOp",EDGE,"E10.MirrorC"),sQuery(id+"F0.wireOp",EDGE,"E11"),sQuery(id+"F0.wireOp",EDGE,"E14.MirrorC"),sQuery(id+"F0.wireOp",EDGE,"E15.MirrorC"),sQuery(id+"F0.wireOp",EDGE,"E17.MirrorC"),sQuery(id+"F0.wireOp",EDGE,"E19.bottom"),sQuery(id+"F0.wireOp",EDGE,"E20.left"),sQuery(id+"F0.wireOp",EDGE,"E21.bottom"),sQuery(id+"F0.wireOp",EDGE,"E22.left")])],"isStart":false}),makeQuery(id+"F7.opExtrude","SWEPT_FACE",FACE,{"disambiguationData":[OSD([sQuery(id+"F6.wireOp",EDGE,"E32.rect.left")])]})]});
            var Q41;
            Q41=makeQuery(id+"F8.opFillet","BLEND_EDGE",EDGE,{"blendedFrom":[makeQuery(id+"F7.boolean.opBoolean","COPY",EDGE,{"derivedFrom":makeQuery(id+"F7.opExtrude","SWEPT_EDGE",EDGE,{"disambiguationData":[OSD([sQuery(id+"F6.wireOp",EDGE,"E32.rect.bottom"),sQuery(id+"F6.wireOp",EDGE,"E32.rect.left")])]})}),makeQuery(id+"F1.opExtrude","CAP_FACE",FACE,{"disambiguationData":[OSD([sQuery(id+"F0.wireOp",EDGE,"E7"),sQuery(id+"F0.wireOp",EDGE,"E8.MirrorC"),sQuery(id+"F0.wireOp",EDGE,"E9.MirrorC"),sQuery(id+"F0.wireOp",EDGE,"E10.MirrorC"),sQuery(id+"F0.wireOp",EDGE,"E11"),sQuery(id+"F0.wireOp",EDGE,"E14.MirrorC"),sQuery(id+"F0.wireOp",EDGE,"E15.MirrorC"),sQuery(id+"F0.wireOp",EDGE,"E17.MirrorC"),sQuery(id+"F0.wireOp",EDGE,"E19.bottom"),sQuery(id+"F0.wireOp",EDGE,"E20.left"),sQuery(id+"F0.wireOp",EDGE,"E21.bottom"),sQuery(id+"F0.wireOp",EDGE,"E22.left")])],"isStart":false})],"blendedInto":[makeQuery(id+"F1.opExtrude","CAP_FACE",FACE,{"disambiguationData":[OSD([sQuery(id+"F0.wireOp",EDGE,"E7"),sQuery(id+"F0.wireOp",EDGE,"E8.MirrorC"),sQuery(id+"F0.wireOp",EDGE,"E9.MirrorC"),sQuery(id+"F0.wireOp",EDGE,"E10.MirrorC"),sQuery(id+"F0.wireOp",EDGE,"E11"),sQuery(id+"F0.wireOp",EDGE,"E14.MirrorC"),sQuery(id+"F0.wireOp",EDGE,"E15.MirrorC"),sQuery(id+"F0.wireOp",EDGE,"E17.MirrorC"),sQuery(id+"F0.wireOp",EDGE,"E19.bottom"),sQuery(id+"F0.wireOp",EDGE,"E20.left"),sQuery(id+"F0.wireOp",EDGE,"E21.bottom"),sQuery(id+"F0.wireOp",EDGE,"E22.left")])],"isStart":false})]});
            var Q42;
            {var subQ0=sQuery(id+"F6.wireOp",EDGE,"E32.rect.bottom");Q42=makeQuery(id+"F7.boolean.opBoolean","INTERSECT",EDGE,{"derivedFrom":[makeQuery(id+"F1.opExtrude","CAP_FACE",FACE,{"disambiguationData":[OSD([sQuery(id+"F0.wireOp",EDGE,"E7"),sQuery(id+"F0.wireOp",EDGE,"E8.MirrorC"),sQuery(id+"F0.wireOp",EDGE,"E9.MirrorC"),sQuery(id+"F0.wireOp",EDGE,"E10.MirrorC"),sQuery(id+"F0.wireOp",EDGE,"E11"),sQuery(id+"F0.wireOp",EDGE,"E14.MirrorC"),sQuery(id+"F0.wireOp",EDGE,"E15.MirrorC"),sQuery(id+"F0.wireOp",EDGE,"E17.MirrorC"),sQuery(id+"F0.wireOp",EDGE,"E19.bottom"),sQuery(id+"F0.wireOp",EDGE,"E20.left"),sQuery(id+"F0.wireOp",EDGE,"E21.bottom"),sQuery(id+"F0.wireOp",EDGE,"E22.left")])],"isStart":false}),makeQuery(id+"F7.opExtrude","SWEPT_FACE",FACE,{"disambiguationData":[OSD([subQ0]),TDD([makeQuery(id+"F6.imprint","IMPRINT",EDGE,{"disambiguationData":[TD([[makeQuery(id+"F6.imprint","INTERSECT",VERTEX,{"derivedFrom":[subQ0,sQuery(id+"F6.wireOp",EDGE,"E32.rect.left")]}),-1.0]])],"derivedFrom":subQ0})])]})]});}
            var Q43;
            {var subQ0=sQuery(id+"F6.wireOp",EDGE,"E30.rect.left");Q43=makeQuery(id+"F7.boolean.opBoolean","INTERSECT",EDGE,{"derivedFrom":[makeQuery(id+"F1.opExtrude","CAP_FACE",FACE,{"disambiguationData":[OSD([sQuery(id+"F0.wireOp",EDGE,"E7"),sQuery(id+"F0.wireOp",EDGE,"E8.MirrorC"),sQuery(id+"F0.wireOp",EDGE,"E9.MirrorC"),sQuery(id+"F0.wireOp",EDGE,"E10.MirrorC"),sQuery(id+"F0.wireOp",EDGE,"E11"),sQuery(id+"F0.wireOp",EDGE,"E14.MirrorC"),sQuery(id+"F0.wireOp",EDGE,"E15.MirrorC"),sQuery(id+"F0.wireOp",EDGE,"E17.MirrorC"),sQuery(id+"F0.wireOp",EDGE,"E19.bottom"),sQuery(id+"F0.wireOp",EDGE,"E20.left"),sQuery(id+"F0.wireOp",EDGE,"E21.bottom"),sQuery(id+"F0.wireOp",EDGE,"E22.left")])],"isStart":false}),makeQuery(id+"F7.opExtrude","SWEPT_FACE",FACE,{"disambiguationData":[OSD([subQ0]),TDD([makeQuery(id+"F6.imprint","IMPRINT",EDGE,{"disambiguationData":[TD([[makeQuery(id+"F6.imprint","INTERSECT",VERTEX,{"derivedFrom":[sQuery(id+"F6.wireOp",EDGE,"E30.rect.bottom"),subQ0]}),-1.0]])],"derivedFrom":subQ0})])]})]});}
            var Q44;
            Q44=makeQuery(id+"F8.opFillet","BLEND_EDGE",EDGE,{"blendedFrom":[makeQuery(id+"F7.boolean.opBoolean","COPY",EDGE,{"derivedFrom":makeQuery(id+"F7.opExtrude","SWEPT_EDGE",EDGE,{"disambiguationData":[OSD([sQuery(id+"F6.wireOp",EDGE,"E30.rect.bottom"),sQuery(id+"F6.wireOp",EDGE,"E30.rect.left")])]})}),makeQuery(id+"F1.opExtrude","CAP_FACE",FACE,{"disambiguationData":[OSD([sQuery(id+"F0.wireOp",EDGE,"E7"),sQuery(id+"F0.wireOp",EDGE,"E8.MirrorC"),sQuery(id+"F0.wireOp",EDGE,"E9.MirrorC"),sQuery(id+"F0.wireOp",EDGE,"E10.MirrorC"),sQuery(id+"F0.wireOp",EDGE,"E11"),sQuery(id+"F0.wireOp",EDGE,"E14.MirrorC"),sQuery(id+"F0.wireOp",EDGE,"E15.MirrorC"),sQuery(id+"F0.wireOp",EDGE,"E17.MirrorC"),sQuery(id+"F0.wireOp",EDGE,"E19.bottom"),sQuery(id+"F0.wireOp",EDGE,"E20.left"),sQuery(id+"F0.wireOp",EDGE,"E21.bottom"),sQuery(id+"F0.wireOp",EDGE,"E22.left")])],"isStart":false})],"blendedInto":[makeQuery(id+"F1.opExtrude","CAP_FACE",FACE,{"disambiguationData":[OSD([sQuery(id+"F0.wireOp",EDGE,"E7"),sQuery(id+"F0.wireOp",EDGE,"E8.MirrorC"),sQuery(id+"F0.wireOp",EDGE,"E9.MirrorC"),sQuery(id+"F0.wireOp",EDGE,"E10.MirrorC"),sQuery(id+"F0.wireOp",EDGE,"E11"),sQuery(id+"F0.wireOp",EDGE,"E14.MirrorC"),sQuery(id+"F0.wireOp",EDGE,"E15.MirrorC"),sQuery(id+"F0.wireOp",EDGE,"E17.MirrorC"),sQuery(id+"F0.wireOp",EDGE,"E19.bottom"),sQuery(id+"F0.wireOp",EDGE,"E20.left"),sQuery(id+"F0.wireOp",EDGE,"E21.bottom"),sQuery(id+"F0.wireOp",EDGE,"E22.left")])],"isStart":false})]});
            var Q45;
            {var subQ0=sQuery(id+"F6.wireOp",EDGE,"E30.rect.bottom");Q45=makeQuery(id+"F7.boolean.opBoolean","INTERSECT",EDGE,{"derivedFrom":[makeQuery(id+"F1.opExtrude","CAP_FACE",FACE,{"disambiguationData":[OSD([sQuery(id+"F0.wireOp",EDGE,"E7"),sQuery(id+"F0.wireOp",EDGE,"E8.MirrorC"),sQuery(id+"F0.wireOp",EDGE,"E9.MirrorC"),sQuery(id+"F0.wireOp",EDGE,"E10.MirrorC"),sQuery(id+"F0.wireOp",EDGE,"E11"),sQuery(id+"F0.wireOp",EDGE,"E14.MirrorC"),sQuery(id+"F0.wireOp",EDGE,"E15.MirrorC"),sQuery(id+"F0.wireOp",EDGE,"E17.MirrorC"),sQuery(id+"F0.wireOp",EDGE,"E19.bottom"),sQuery(id+"F0.wireOp",EDGE,"E20.left"),sQuery(id+"F0.wireOp",EDGE,"E21.bottom"),sQuery(id+"F0.wireOp",EDGE,"E22.left")])],"isStart":false}),makeQuery(id+"F7.opExtrude","SWEPT_FACE",FACE,{"disambiguationData":[OSD([subQ0]),TDD([makeQuery(id+"F6.imprint","IMPRINT",EDGE,{"disambiguationData":[TD([[makeQuery(id+"F6.imprint","INTERSECT",VERTEX,{"derivedFrom":[subQ0,sQuery(id+"F6.wireOp",EDGE,"E30.rect.left")]}),-1.0]])],"derivedFrom":subQ0})])]})]});}
            var Q46;
            {var subQ0=sQuery(id+"F6.wireOp",EDGE,"E31.rect.right");Q46=makeQuery(id+"F7.boolean.opBoolean","INTERSECT",EDGE,{"derivedFrom":[makeQuery(id+"F1.opExtrude","CAP_FACE",FACE,{"disambiguationData":[OSD([sQuery(id+"F0.wireOp",EDGE,"E7"),sQuery(id+"F0.wireOp",EDGE,"E8.MirrorC"),sQuery(id+"F0.wireOp",EDGE,"E9.MirrorC"),sQuery(id+"F0.wireOp",EDGE,"E10.MirrorC"),sQuery(id+"F0.wireOp",EDGE,"E11"),sQuery(id+"F0.wireOp",EDGE,"E14.MirrorC"),sQuery(id+"F0.wireOp",EDGE,"E15.MirrorC"),sQuery(id+"F0.wireOp",EDGE,"E17.MirrorC"),sQuery(id+"F0.wireOp",EDGE,"E19.bottom"),sQuery(id+"F0.wireOp",EDGE,"E20.left"),sQuery(id+"F0.wireOp",EDGE,"E21.bottom"),sQuery(id+"F0.wireOp",EDGE,"E22.left")])],"isStart":false}),makeQuery(id+"F7.opExtrude","SWEPT_FACE",FACE,{"disambiguationData":[OSD([subQ0]),TDD([makeQuery(id+"F6.imprint","IMPRINT",EDGE,{"disambiguationData":[TD([[makeQuery(id+"F6.imprint","INTERSECT",VERTEX,{"derivedFrom":[sQuery(id+"F6.wireOp",EDGE,"E31.rect.top"),subQ0]}),1.0]])],"derivedFrom":subQ0})])]})]});}
            var Q47;
            Q47=makeQuery(id+"F7.boolean.opBoolean","INTERSECT",EDGE,{"derivedFrom":[makeQuery(id+"F1.opExtrude","CAP_FACE",FACE,{"disambiguationData":[OSD([sQuery(id+"F0.wireOp",EDGE,"E7"),sQuery(id+"F0.wireOp",EDGE,"E8.MirrorC"),sQuery(id+"F0.wireOp",EDGE,"E9.MirrorC"),sQuery(id+"F0.wireOp",EDGE,"E10.MirrorC"),sQuery(id+"F0.wireOp",EDGE,"E11"),sQuery(id+"F0.wireOp",EDGE,"E14.MirrorC"),sQuery(id+"F0.wireOp",EDGE,"E15.MirrorC"),sQuery(id+"F0.wireOp",EDGE,"E17.MirrorC"),sQuery(id+"F0.wireOp",EDGE,"E19.bottom"),sQuery(id+"F0.wireOp",EDGE,"E20.left"),sQuery(id+"F0.wireOp",EDGE,"E21.bottom"),sQuery(id+"F0.wireOp",EDGE,"E22.left")])],"isStart":false}),makeQuery(id+"F7.opExtrude","SWEPT_FACE",FACE,{"disambiguationData":[OSD([sQuery(id+"F6.wireOp",EDGE,"E31.rect.top")])]})]});
            var Q48;
            Q48=makeQuery(id+"F8.opFillet","BLEND_EDGE",EDGE,{"blendedFrom":[makeQuery(id+"F7.boolean.opBoolean","COPY",EDGE,{"derivedFrom":makeQuery(id+"F7.opExtrude","SWEPT_EDGE",EDGE,{"disambiguationData":[OSD([sQuery(id+"F6.wireOp",EDGE,"E31.rect.top"),sQuery(id+"F6.wireOp",EDGE,"E31.rect.left")])]})}),makeQuery(id+"F1.opExtrude","CAP_FACE",FACE,{"disambiguationData":[OSD([sQuery(id+"F0.wireOp",EDGE,"E7"),sQuery(id+"F0.wireOp",EDGE,"E8.MirrorC"),sQuery(id+"F0.wireOp",EDGE,"E9.MirrorC"),sQuery(id+"F0.wireOp",EDGE,"E10.MirrorC"),sQuery(id+"F0.wireOp",EDGE,"E11"),sQuery(id+"F0.wireOp",EDGE,"E14.MirrorC"),sQuery(id+"F0.wireOp",EDGE,"E15.MirrorC"),sQuery(id+"F0.wireOp",EDGE,"E17.MirrorC"),sQuery(id+"F0.wireOp",EDGE,"E19.bottom"),sQuery(id+"F0.wireOp",EDGE,"E20.left"),sQuery(id+"F0.wireOp",EDGE,"E21.bottom"),sQuery(id+"F0.wireOp",EDGE,"E22.left")])],"isStart":false})],"blendedInto":[makeQuery(id+"F1.opExtrude","CAP_FACE",FACE,{"disambiguationData":[OSD([sQuery(id+"F0.wireOp",EDGE,"E7"),sQuery(id+"F0.wireOp",EDGE,"E8.MirrorC"),sQuery(id+"F0.wireOp",EDGE,"E9.MirrorC"),sQuery(id+"F0.wireOp",EDGE,"E10.MirrorC"),sQuery(id+"F0.wireOp",EDGE,"E11"),sQuery(id+"F0.wireOp",EDGE,"E14.MirrorC"),sQuery(id+"F0.wireOp",EDGE,"E15.MirrorC"),sQuery(id+"F0.wireOp",EDGE,"E17.MirrorC"),sQuery(id+"F0.wireOp",EDGE,"E19.bottom"),sQuery(id+"F0.wireOp",EDGE,"E20.left"),sQuery(id+"F0.wireOp",EDGE,"E21.bottom"),sQuery(id+"F0.wireOp",EDGE,"E22.left")])],"isStart":false})]});
            var Q49;
            {var subQ0=sQuery(id+"F6.wireOp",EDGE,"E31.rect.left");Q49=makeQuery(id+"F7.boolean.opBoolean","INTERSECT",EDGE,{"derivedFrom":[makeQuery(id+"F1.opExtrude","CAP_FACE",FACE,{"disambiguationData":[OSD([sQuery(id+"F0.wireOp",EDGE,"E7"),sQuery(id+"F0.wireOp",EDGE,"E8.MirrorC"),sQuery(id+"F0.wireOp",EDGE,"E9.MirrorC"),sQuery(id+"F0.wireOp",EDGE,"E10.MirrorC"),sQuery(id+"F0.wireOp",EDGE,"E11"),sQuery(id+"F0.wireOp",EDGE,"E14.MirrorC"),sQuery(id+"F0.wireOp",EDGE,"E15.MirrorC"),sQuery(id+"F0.wireOp",EDGE,"E17.MirrorC"),sQuery(id+"F0.wireOp",EDGE,"E19.bottom"),sQuery(id+"F0.wireOp",EDGE,"E20.left"),sQuery(id+"F0.wireOp",EDGE,"E21.bottom"),sQuery(id+"F0.wireOp",EDGE,"E22.left")])],"isStart":false}),makeQuery(id+"F7.opExtrude","SWEPT_FACE",FACE,{"disambiguationData":[OSD([subQ0]),TDD([makeQuery(id+"F6.imprint","IMPRINT",EDGE,{"disambiguationData":[TD([[makeQuery(id+"F6.imprint","INTERSECT",VERTEX,{"derivedFrom":[sQuery(id+"F6.wireOp",EDGE,"E31.rect.top"),subQ0]}),1.0]])],"derivedFrom":subQ0})])]})]});}
            var Q50;
            Q50=makeQuery(id+"F8.opFillet","BLEND_EDGE",EDGE,{"blendedFrom":[makeQuery(id+"F7.boolean.opBoolean","COPY",EDGE,{"derivedFrom":makeQuery(id+"F7.opExtrude","SWEPT_EDGE",EDGE,{"disambiguationData":[OSD([sQuery(id+"F6.wireOp",EDGE,"E31.rect.top"),sQuery(id+"F6.wireOp",EDGE,"E31.rect.right")])]})}),makeQuery(id+"F1.opExtrude","CAP_FACE",FACE,{"disambiguationData":[OSD([sQuery(id+"F0.wireOp",EDGE,"E7"),sQuery(id+"F0.wireOp",EDGE,"E8.MirrorC"),sQuery(id+"F0.wireOp",EDGE,"E9.MirrorC"),sQuery(id+"F0.wireOp",EDGE,"E10.MirrorC"),sQuery(id+"F0.wireOp",EDGE,"E11"),sQuery(id+"F0.wireOp",EDGE,"E14.MirrorC"),sQuery(id+"F0.wireOp",EDGE,"E15.MirrorC"),sQuery(id+"F0.wireOp",EDGE,"E17.MirrorC"),sQuery(id+"F0.wireOp",EDGE,"E19.bottom"),sQuery(id+"F0.wireOp",EDGE,"E20.left"),sQuery(id+"F0.wireOp",EDGE,"E21.bottom"),sQuery(id+"F0.wireOp",EDGE,"E22.left")])],"isStart":false})],"blendedInto":[makeQuery(id+"F1.opExtrude","CAP_FACE",FACE,{"disambiguationData":[OSD([sQuery(id+"F0.wireOp",EDGE,"E7"),sQuery(id+"F0.wireOp",EDGE,"E8.MirrorC"),sQuery(id+"F0.wireOp",EDGE,"E9.MirrorC"),sQuery(id+"F0.wireOp",EDGE,"E10.MirrorC"),sQuery(id+"F0.wireOp",EDGE,"E11"),sQuery(id+"F0.wireOp",EDGE,"E14.MirrorC"),sQuery(id+"F0.wireOp",EDGE,"E15.MirrorC"),sQuery(id+"F0.wireOp",EDGE,"E17.MirrorC"),sQuery(id+"F0.wireOp",EDGE,"E19.bottom"),sQuery(id+"F0.wireOp",EDGE,"E20.left"),sQuery(id+"F0.wireOp",EDGE,"E21.bottom"),sQuery(id+"F0.wireOp",EDGE,"E22.left")])],"isStart":false})]});
            var Q51;
            {var subQ0=sQuery(id+"F6.wireOp",EDGE,"E30.rect.bottom");Q51=makeQuery(id+"F7.boolean.opBoolean","INTERSECT",EDGE,{"derivedFrom":[makeQuery(id+"F1.opExtrude","CAP_FACE",FACE,{"disambiguationData":[OSD([sQuery(id+"F0.wireOp",EDGE,"E7"),sQuery(id+"F0.wireOp",EDGE,"E8.MirrorC"),sQuery(id+"F0.wireOp",EDGE,"E9.MirrorC"),sQuery(id+"F0.wireOp",EDGE,"E10.MirrorC"),sQuery(id+"F0.wireOp",EDGE,"E11"),sQuery(id+"F0.wireOp",EDGE,"E14.MirrorC"),sQuery(id+"F0.wireOp",EDGE,"E15.MirrorC"),sQuery(id+"F0.wireOp",EDGE,"E17.MirrorC"),sQuery(id+"F0.wireOp",EDGE,"E19.bottom"),sQuery(id+"F0.wireOp",EDGE,"E20.left"),sQuery(id+"F0.wireOp",EDGE,"E21.bottom"),sQuery(id+"F0.wireOp",EDGE,"E22.left")])],"isStart":false}),makeQuery(id+"F7.opExtrude","SWEPT_FACE",FACE,{"disambiguationData":[OSD([subQ0]),TDD([makeQuery(id+"F6.imprint","IMPRINT",EDGE,{"disambiguationData":[TD([[makeQuery(id+"F6.imprint","INTERSECT",VERTEX,{"derivedFrom":[subQ0,sQuery(id+"F6.wireOp",EDGE,"E30.rect.right")]}),1.0]])],"derivedFrom":subQ0})])]})]});}
            var Q52;
            Q52=makeQuery(id+"F8.opFillet","BLEND_EDGE",EDGE,{"blendedFrom":[makeQuery(id+"F7.boolean.opBoolean","COPY",EDGE,{"derivedFrom":makeQuery(id+"F7.opExtrude","SWEPT_EDGE",EDGE,{"disambiguationData":[OSD([sQuery(id+"F6.wireOp",EDGE,"E30.rect.bottom"),sQuery(id+"F6.wireOp",EDGE,"E30.rect.right")])]})}),makeQuery(id+"F1.opExtrude","CAP_FACE",FACE,{"disambiguationData":[OSD([sQuery(id+"F0.wireOp",EDGE,"E7"),sQuery(id+"F0.wireOp",EDGE,"E8.MirrorC"),sQuery(id+"F0.wireOp",EDGE,"E9.MirrorC"),sQuery(id+"F0.wireOp",EDGE,"E10.MirrorC"),sQuery(id+"F0.wireOp",EDGE,"E11"),sQuery(id+"F0.wireOp",EDGE,"E14.MirrorC"),sQuery(id+"F0.wireOp",EDGE,"E15.MirrorC"),sQuery(id+"F0.wireOp",EDGE,"E17.MirrorC"),sQuery(id+"F0.wireOp",EDGE,"E19.bottom"),sQuery(id+"F0.wireOp",EDGE,"E20.left"),sQuery(id+"F0.wireOp",EDGE,"E21.bottom"),sQuery(id+"F0.wireOp",EDGE,"E22.left")])],"isStart":false})],"blendedInto":[makeQuery(id+"F1.opExtrude","CAP_FACE",FACE,{"disambiguationData":[OSD([sQuery(id+"F0.wireOp",EDGE,"E7"),sQuery(id+"F0.wireOp",EDGE,"E8.MirrorC"),sQuery(id+"F0.wireOp",EDGE,"E9.MirrorC"),sQuery(id+"F0.wireOp",EDGE,"E10.MirrorC"),sQuery(id+"F0.wireOp",EDGE,"E11"),sQuery(id+"F0.wireOp",EDGE,"E14.MirrorC"),sQuery(id+"F0.wireOp",EDGE,"E15.MirrorC"),sQuery(id+"F0.wireOp",EDGE,"E17.MirrorC"),sQuery(id+"F0.wireOp",EDGE,"E19.bottom"),sQuery(id+"F0.wireOp",EDGE,"E20.left"),sQuery(id+"F0.wireOp",EDGE,"E21.bottom"),sQuery(id+"F0.wireOp",EDGE,"E22.left")])],"isStart":false})]});
            var Q53;
            {var subQ0=sQuery(id+"F6.wireOp",EDGE,"E30.rect.right");Q53=makeQuery(id+"F7.boolean.opBoolean","INTERSECT",EDGE,{"derivedFrom":[makeQuery(id+"F1.opExtrude","CAP_FACE",FACE,{"disambiguationData":[OSD([sQuery(id+"F0.wireOp",EDGE,"E7"),sQuery(id+"F0.wireOp",EDGE,"E8.MirrorC"),sQuery(id+"F0.wireOp",EDGE,"E9.MirrorC"),sQuery(id+"F0.wireOp",EDGE,"E10.MirrorC"),sQuery(id+"F0.wireOp",EDGE,"E11"),sQuery(id+"F0.wireOp",EDGE,"E14.MirrorC"),sQuery(id+"F0.wireOp",EDGE,"E15.MirrorC"),sQuery(id+"F0.wireOp",EDGE,"E17.MirrorC"),sQuery(id+"F0.wireOp",EDGE,"E19.bottom"),sQuery(id+"F0.wireOp",EDGE,"E20.left"),sQuery(id+"F0.wireOp",EDGE,"E21.bottom"),sQuery(id+"F0.wireOp",EDGE,"E22.left")])],"isStart":false}),makeQuery(id+"F7.opExtrude","SWEPT_FACE",FACE,{"disambiguationData":[OSD([subQ0]),TDD([makeQuery(id+"F6.imprint","IMPRINT",EDGE,{"disambiguationData":[TD([[makeQuery(id+"F6.imprint","INTERSECT",VERTEX,{"derivedFrom":[sQuery(id+"F6.wireOp",EDGE,"E30.rect.bottom"),subQ0]}),-1.0]])],"derivedFrom":subQ0})])]})]});}
            var Q54;
            {var subQ0=sQuery(id+"F6.wireOp",EDGE,"E32.rect.bottom");Q54=makeQuery(id+"F7.boolean.opBoolean","INTERSECT",EDGE,{"derivedFrom":[makeQuery(id+"F1.opExtrude","CAP_FACE",FACE,{"disambiguationData":[OSD([sQuery(id+"F0.wireOp",EDGE,"E7"),sQuery(id+"F0.wireOp",EDGE,"E8.MirrorC"),sQuery(id+"F0.wireOp",EDGE,"E9.MirrorC"),sQuery(id+"F0.wireOp",EDGE,"E10.MirrorC"),sQuery(id+"F0.wireOp",EDGE,"E11"),sQuery(id+"F0.wireOp",EDGE,"E14.MirrorC"),sQuery(id+"F0.wireOp",EDGE,"E15.MirrorC"),sQuery(id+"F0.wireOp",EDGE,"E17.MirrorC"),sQuery(id+"F0.wireOp",EDGE,"E19.bottom"),sQuery(id+"F0.wireOp",EDGE,"E20.left"),sQuery(id+"F0.wireOp",EDGE,"E21.bottom"),sQuery(id+"F0.wireOp",EDGE,"E22.left")])],"isStart":false}),makeQuery(id+"F7.opExtrude","SWEPT_FACE",FACE,{"disambiguationData":[OSD([subQ0]),TDD([makeQuery(id+"F6.imprint","IMPRINT",EDGE,{"disambiguationData":[TD([[makeQuery(id+"F6.imprint","INTERSECT",VERTEX,{"derivedFrom":[subQ0,sQuery(id+"F6.wireOp",EDGE,"E32.rect.right")]}),1.0]])],"derivedFrom":subQ0})])]})]});}
            var Q55;
            Q55=makeQuery(id+"F8.opFillet","BLEND_EDGE",EDGE,{"blendedFrom":[makeQuery(id+"F7.boolean.opBoolean","COPY",EDGE,{"derivedFrom":makeQuery(id+"F7.opExtrude","SWEPT_EDGE",EDGE,{"disambiguationData":[OSD([sQuery(id+"F6.wireOp",EDGE,"E32.rect.bottom"),sQuery(id+"F6.wireOp",EDGE,"E32.rect.right")])]})}),makeQuery(id+"F1.opExtrude","CAP_FACE",FACE,{"disambiguationData":[OSD([sQuery(id+"F0.wireOp",EDGE,"E7"),sQuery(id+"F0.wireOp",EDGE,"E8.MirrorC"),sQuery(id+"F0.wireOp",EDGE,"E9.MirrorC"),sQuery(id+"F0.wireOp",EDGE,"E10.MirrorC"),sQuery(id+"F0.wireOp",EDGE,"E11"),sQuery(id+"F0.wireOp",EDGE,"E14.MirrorC"),sQuery(id+"F0.wireOp",EDGE,"E15.MirrorC"),sQuery(id+"F0.wireOp",EDGE,"E17.MirrorC"),sQuery(id+"F0.wireOp",EDGE,"E19.bottom"),sQuery(id+"F0.wireOp",EDGE,"E20.left"),sQuery(id+"F0.wireOp",EDGE,"E21.bottom"),sQuery(id+"F0.wireOp",EDGE,"E22.left")])],"isStart":false})],"blendedInto":[makeQuery(id+"F1.opExtrude","CAP_FACE",FACE,{"disambiguationData":[OSD([sQuery(id+"F0.wireOp",EDGE,"E7"),sQuery(id+"F0.wireOp",EDGE,"E8.MirrorC"),sQuery(id+"F0.wireOp",EDGE,"E9.MirrorC"),sQuery(id+"F0.wireOp",EDGE,"E10.MirrorC"),sQuery(id+"F0.wireOp",EDGE,"E11"),sQuery(id+"F0.wireOp",EDGE,"E14.MirrorC"),sQuery(id+"F0.wireOp",EDGE,"E15.MirrorC"),sQuery(id+"F0.wireOp",EDGE,"E17.MirrorC"),sQuery(id+"F0.wireOp",EDGE,"E19.bottom"),sQuery(id+"F0.wireOp",EDGE,"E20.left"),sQuery(id+"F0.wireOp",EDGE,"E21.bottom"),sQuery(id+"F0.wireOp",EDGE,"E22.left")])],"isStart":false})]});
            var Q56;
            Q56=makeQuery(id+"F7.boolean.opBoolean","INTERSECT",EDGE,{"derivedFrom":[makeQuery(id+"F1.opExtrude","CAP_FACE",FACE,{"disambiguationData":[OSD([sQuery(id+"F0.wireOp",EDGE,"E7"),sQuery(id+"F0.wireOp",EDGE,"E8.MirrorC"),sQuery(id+"F0.wireOp",EDGE,"E9.MirrorC"),sQuery(id+"F0.wireOp",EDGE,"E10.MirrorC"),sQuery(id+"F0.wireOp",EDGE,"E11"),sQuery(id+"F0.wireOp",EDGE,"E14.MirrorC"),sQuery(id+"F0.wireOp",EDGE,"E15.MirrorC"),sQuery(id+"F0.wireOp",EDGE,"E17.MirrorC"),sQuery(id+"F0.wireOp",EDGE,"E19.bottom"),sQuery(id+"F0.wireOp",EDGE,"E20.left"),sQuery(id+"F0.wireOp",EDGE,"E21.bottom"),sQuery(id+"F0.wireOp",EDGE,"E22.left")])],"isStart":false}),makeQuery(id+"F7.opExtrude","SWEPT_FACE",FACE,{"disambiguationData":[OSD([sQuery(id+"F6.wireOp",EDGE,"E32.rect.right")])]})]});
            var Q57;
            Q57=makeQuery(id+"F8.opFillet","BLEND_EDGE",EDGE,{"blendedFrom":[makeQuery(id+"F7.boolean.opBoolean","COPY",EDGE,{"derivedFrom":makeQuery(id+"F7.opExtrude","SWEPT_EDGE",EDGE,{"disambiguationData":[OSD([sQuery(id+"F6.wireOp",EDGE,"E32.rect.top"),sQuery(id+"F6.wireOp",EDGE,"E32.rect.right")])]})}),makeQuery(id+"F1.opExtrude","CAP_FACE",FACE,{"disambiguationData":[OSD([sQuery(id+"F0.wireOp",EDGE,"E7"),sQuery(id+"F0.wireOp",EDGE,"E8.MirrorC"),sQuery(id+"F0.wireOp",EDGE,"E9.MirrorC"),sQuery(id+"F0.wireOp",EDGE,"E10.MirrorC"),sQuery(id+"F0.wireOp",EDGE,"E11"),sQuery(id+"F0.wireOp",EDGE,"E14.MirrorC"),sQuery(id+"F0.wireOp",EDGE,"E15.MirrorC"),sQuery(id+"F0.wireOp",EDGE,"E17.MirrorC"),sQuery(id+"F0.wireOp",EDGE,"E19.bottom"),sQuery(id+"F0.wireOp",EDGE,"E20.left"),sQuery(id+"F0.wireOp",EDGE,"E21.bottom"),sQuery(id+"F0.wireOp",EDGE,"E22.left")])],"isStart":false})],"blendedInto":[makeQuery(id+"F1.opExtrude","CAP_FACE",FACE,{"disambiguationData":[OSD([sQuery(id+"F0.wireOp",EDGE,"E7"),sQuery(id+"F0.wireOp",EDGE,"E8.MirrorC"),sQuery(id+"F0.wireOp",EDGE,"E9.MirrorC"),sQuery(id+"F0.wireOp",EDGE,"E10.MirrorC"),sQuery(id+"F0.wireOp",EDGE,"E11"),sQuery(id+"F0.wireOp",EDGE,"E14.MirrorC"),sQuery(id+"F0.wireOp",EDGE,"E15.MirrorC"),sQuery(id+"F0.wireOp",EDGE,"E17.MirrorC"),sQuery(id+"F0.wireOp",EDGE,"E19.bottom"),sQuery(id+"F0.wireOp",EDGE,"E20.left"),sQuery(id+"F0.wireOp",EDGE,"E21.bottom"),sQuery(id+"F0.wireOp",EDGE,"E22.left")])],"isStart":false})]});
            var Q58;
            {var subQ0=sQuery(id+"F6.wireOp",EDGE,"E32.rect.top");Q58=makeQuery(id+"F7.boolean.opBoolean","INTERSECT",EDGE,{"derivedFrom":[makeQuery(id+"F1.opExtrude","CAP_FACE",FACE,{"disambiguationData":[OSD([sQuery(id+"F0.wireOp",EDGE,"E7"),sQuery(id+"F0.wireOp",EDGE,"E8.MirrorC"),sQuery(id+"F0.wireOp",EDGE,"E9.MirrorC"),sQuery(id+"F0.wireOp",EDGE,"E10.MirrorC"),sQuery(id+"F0.wireOp",EDGE,"E11"),sQuery(id+"F0.wireOp",EDGE,"E14.MirrorC"),sQuery(id+"F0.wireOp",EDGE,"E15.MirrorC"),sQuery(id+"F0.wireOp",EDGE,"E17.MirrorC"),sQuery(id+"F0.wireOp",EDGE,"E19.bottom"),sQuery(id+"F0.wireOp",EDGE,"E20.left"),sQuery(id+"F0.wireOp",EDGE,"E21.bottom"),sQuery(id+"F0.wireOp",EDGE,"E22.left")])],"isStart":false}),makeQuery(id+"F7.opExtrude","SWEPT_FACE",FACE,{"disambiguationData":[OSD([subQ0]),TDD([makeQuery(id+"F6.imprint","IMPRINT",EDGE,{"disambiguationData":[TD([[makeQuery(id+"F6.imprint","INTERSECT",VERTEX,{"derivedFrom":[subQ0,sQuery(id+"F6.wireOp",EDGE,"E32.rect.right")]}),1.0]])],"derivedFrom":subQ0})])]})]});}
            var Q59;
            {var subQ0=sQuery(id+"F6.wireOp",EDGE,"E30.rect.right");Q59=makeQuery(id+"F7.boolean.opBoolean","INTERSECT",EDGE,{"derivedFrom":[makeQuery(id+"F1.opExtrude","CAP_FACE",FACE,{"disambiguationData":[OSD([sQuery(id+"F0.wireOp",EDGE,"E7"),sQuery(id+"F0.wireOp",EDGE,"E8.MirrorC"),sQuery(id+"F0.wireOp",EDGE,"E9.MirrorC"),sQuery(id+"F0.wireOp",EDGE,"E10.MirrorC"),sQuery(id+"F0.wireOp",EDGE,"E11"),sQuery(id+"F0.wireOp",EDGE,"E14.MirrorC"),sQuery(id+"F0.wireOp",EDGE,"E15.MirrorC"),sQuery(id+"F0.wireOp",EDGE,"E17.MirrorC"),sQuery(id+"F0.wireOp",EDGE,"E19.bottom"),sQuery(id+"F0.wireOp",EDGE,"E20.left"),sQuery(id+"F0.wireOp",EDGE,"E21.bottom"),sQuery(id+"F0.wireOp",EDGE,"E22.left")])],"isStart":false}),makeQuery(id+"F7.opExtrude","SWEPT_FACE",FACE,{"disambiguationData":[OSD([subQ0]),TDD([makeQuery(id+"F6.imprint","IMPRINT",EDGE,{"disambiguationData":[TD([[makeQuery(id+"F6.imprint","INTERSECT",VERTEX,{"derivedFrom":[sQuery(id+"F6.wireOp",EDGE,"E30.rect.top"),subQ0]}),1.0]])],"derivedFrom":subQ0})])]})]});}
            var Q60;
            Q60=makeQuery(id+"F8.opFillet","BLEND_EDGE",EDGE,{"blendedFrom":[makeQuery(id+"F7.boolean.opBoolean","COPY",EDGE,{"derivedFrom":makeQuery(id+"F7.opExtrude","SWEPT_EDGE",EDGE,{"disambiguationData":[OSD([sQuery(id+"F6.wireOp",EDGE,"E30.rect.top"),sQuery(id+"F6.wireOp",EDGE,"E30.rect.right")])]})}),makeQuery(id+"F1.opExtrude","CAP_FACE",FACE,{"disambiguationData":[OSD([sQuery(id+"F0.wireOp",EDGE,"E7"),sQuery(id+"F0.wireOp",EDGE,"E8.MirrorC"),sQuery(id+"F0.wireOp",EDGE,"E9.MirrorC"),sQuery(id+"F0.wireOp",EDGE,"E10.MirrorC"),sQuery(id+"F0.wireOp",EDGE,"E11"),sQuery(id+"F0.wireOp",EDGE,"E14.MirrorC"),sQuery(id+"F0.wireOp",EDGE,"E15.MirrorC"),sQuery(id+"F0.wireOp",EDGE,"E17.MirrorC"),sQuery(id+"F0.wireOp",EDGE,"E19.bottom"),sQuery(id+"F0.wireOp",EDGE,"E20.left"),sQuery(id+"F0.wireOp",EDGE,"E21.bottom"),sQuery(id+"F0.wireOp",EDGE,"E22.left")])],"isStart":false})],"blendedInto":[makeQuery(id+"F1.opExtrude","CAP_FACE",FACE,{"disambiguationData":[OSD([sQuery(id+"F0.wireOp",EDGE,"E7"),sQuery(id+"F0.wireOp",EDGE,"E8.MirrorC"),sQuery(id+"F0.wireOp",EDGE,"E9.MirrorC"),sQuery(id+"F0.wireOp",EDGE,"E10.MirrorC"),sQuery(id+"F0.wireOp",EDGE,"E11"),sQuery(id+"F0.wireOp",EDGE,"E14.MirrorC"),sQuery(id+"F0.wireOp",EDGE,"E15.MirrorC"),sQuery(id+"F0.wireOp",EDGE,"E17.MirrorC"),sQuery(id+"F0.wireOp",EDGE,"E19.bottom"),sQuery(id+"F0.wireOp",EDGE,"E20.left"),sQuery(id+"F0.wireOp",EDGE,"E21.bottom"),sQuery(id+"F0.wireOp",EDGE,"E22.left")])],"isStart":false})]});
            var Q61;
            {var subQ0=sQuery(id+"F6.wireOp",EDGE,"E30.rect.top");Q61=makeQuery(id+"F7.boolean.opBoolean","INTERSECT",EDGE,{"derivedFrom":[makeQuery(id+"F1.opExtrude","CAP_FACE",FACE,{"disambiguationData":[OSD([sQuery(id+"F0.wireOp",EDGE,"E7"),sQuery(id+"F0.wireOp",EDGE,"E8.MirrorC"),sQuery(id+"F0.wireOp",EDGE,"E9.MirrorC"),sQuery(id+"F0.wireOp",EDGE,"E10.MirrorC"),sQuery(id+"F0.wireOp",EDGE,"E11"),sQuery(id+"F0.wireOp",EDGE,"E14.MirrorC"),sQuery(id+"F0.wireOp",EDGE,"E15.MirrorC"),sQuery(id+"F0.wireOp",EDGE,"E17.MirrorC"),sQuery(id+"F0.wireOp",EDGE,"E19.bottom"),sQuery(id+"F0.wireOp",EDGE,"E20.left"),sQuery(id+"F0.wireOp",EDGE,"E21.bottom"),sQuery(id+"F0.wireOp",EDGE,"E22.left")])],"isStart":false}),makeQuery(id+"F7.opExtrude","SWEPT_FACE",FACE,{"disambiguationData":[OSD([subQ0]),TDD([makeQuery(id+"F6.imprint","IMPRINT",EDGE,{"disambiguationData":[TD([[makeQuery(id+"F6.imprint","INTERSECT",VERTEX,{"derivedFrom":[subQ0,sQuery(id+"F6.wireOp",EDGE,"E30.rect.right")]}),1.0]])],"derivedFrom":subQ0})])]})]});}
            var Q62;
            {var subQ0=sQuery(id+"F6.wireOp",EDGE,"E31.rect.left");Q62=makeQuery(id+"F7.boolean.opBoolean","INTERSECT",EDGE,{"derivedFrom":[makeQuery(id+"F1.opExtrude","CAP_FACE",FACE,{"disambiguationData":[OSD([sQuery(id+"F0.wireOp",EDGE,"E7"),sQuery(id+"F0.wireOp",EDGE,"E8.MirrorC"),sQuery(id+"F0.wireOp",EDGE,"E9.MirrorC"),sQuery(id+"F0.wireOp",EDGE,"E10.MirrorC"),sQuery(id+"F0.wireOp",EDGE,"E11"),sQuery(id+"F0.wireOp",EDGE,"E14.MirrorC"),sQuery(id+"F0.wireOp",EDGE,"E15.MirrorC"),sQuery(id+"F0.wireOp",EDGE,"E17.MirrorC"),sQuery(id+"F0.wireOp",EDGE,"E19.bottom"),sQuery(id+"F0.wireOp",EDGE,"E20.left"),sQuery(id+"F0.wireOp",EDGE,"E21.bottom"),sQuery(id+"F0.wireOp",EDGE,"E22.left")])],"isStart":false}),makeQuery(id+"F7.opExtrude","SWEPT_FACE",FACE,{"disambiguationData":[OSD([subQ0]),TDD([makeQuery(id+"F6.imprint","IMPRINT",EDGE,{"disambiguationData":[TD([[makeQuery(id+"F6.imprint","INTERSECT",VERTEX,{"derivedFrom":[sQuery(id+"F6.wireOp",EDGE,"E31.rect.bottom"),subQ0]}),-1.0]])],"derivedFrom":subQ0})])]})]});}
            var Q63;
            Q63=makeQuery(id+"F8.opFillet","BLEND_EDGE",EDGE,{"blendedFrom":[makeQuery(id+"F7.boolean.opBoolean","COPY",EDGE,{"derivedFrom":makeQuery(id+"F7.opExtrude","SWEPT_EDGE",EDGE,{"disambiguationData":[OSD([sQuery(id+"F6.wireOp",EDGE,"E31.rect.bottom"),sQuery(id+"F6.wireOp",EDGE,"E31.rect.left")])]})}),makeQuery(id+"F1.opExtrude","CAP_FACE",FACE,{"disambiguationData":[OSD([sQuery(id+"F0.wireOp",EDGE,"E7"),sQuery(id+"F0.wireOp",EDGE,"E8.MirrorC"),sQuery(id+"F0.wireOp",EDGE,"E9.MirrorC"),sQuery(id+"F0.wireOp",EDGE,"E10.MirrorC"),sQuery(id+"F0.wireOp",EDGE,"E11"),sQuery(id+"F0.wireOp",EDGE,"E14.MirrorC"),sQuery(id+"F0.wireOp",EDGE,"E15.MirrorC"),sQuery(id+"F0.wireOp",EDGE,"E17.MirrorC"),sQuery(id+"F0.wireOp",EDGE,"E19.bottom"),sQuery(id+"F0.wireOp",EDGE,"E20.left"),sQuery(id+"F0.wireOp",EDGE,"E21.bottom"),sQuery(id+"F0.wireOp",EDGE,"E22.left")])],"isStart":false})],"blendedInto":[makeQuery(id+"F1.opExtrude","CAP_FACE",FACE,{"disambiguationData":[OSD([sQuery(id+"F0.wireOp",EDGE,"E7"),sQuery(id+"F0.wireOp",EDGE,"E8.MirrorC"),sQuery(id+"F0.wireOp",EDGE,"E9.MirrorC"),sQuery(id+"F0.wireOp",EDGE,"E10.MirrorC"),sQuery(id+"F0.wireOp",EDGE,"E11"),sQuery(id+"F0.wireOp",EDGE,"E14.MirrorC"),sQuery(id+"F0.wireOp",EDGE,"E15.MirrorC"),sQuery(id+"F0.wireOp",EDGE,"E17.MirrorC"),sQuery(id+"F0.wireOp",EDGE,"E19.bottom"),sQuery(id+"F0.wireOp",EDGE,"E20.left"),sQuery(id+"F0.wireOp",EDGE,"E21.bottom"),sQuery(id+"F0.wireOp",EDGE,"E22.left")])],"isStart":false})]});
            var Q64;
            Q64=makeQuery(id+"F7.boolean.opBoolean","COPY",EDGE,{"derivedFrom":makeQuery(id+"F7.opExtrude","SWEPT_EDGE",EDGE,{"disambiguationData":[OSD([sQuery(id+"F6.wireOp",EDGE,"E30.rect.top"),sQuery(id+"F6.wireOp",EDGE,"E31.rect.left")])]})});
            var Q65;
            Q65=makeQuery(id+"F7.boolean.opBoolean","COPY",EDGE,{"derivedFrom":makeQuery(id+"F7.opExtrude","SWEPT_EDGE",EDGE,{"disambiguationData":[OSD([sQuery(id+"F6.wireOp",EDGE,"E30.rect.right"),sQuery(id+"F6.wireOp",EDGE,"E32.rect.bottom")])]})});
            var Q66;
            Q66=makeQuery(id+"F7.boolean.opBoolean","COPY",EDGE,{"derivedFrom":makeQuery(id+"F7.opExtrude","SWEPT_EDGE",EDGE,{"disambiguationData":[OSD([sQuery(id+"F6.wireOp",EDGE,"E30.rect.top"),sQuery(id+"F6.wireOp",EDGE,"E31.rect.right")])]})});
            var Q67;
            Q67=makeQuery(id+"F7.boolean.opBoolean","COPY",EDGE,{"derivedFrom":makeQuery(id+"F7.opExtrude","SWEPT_EDGE",EDGE,{"disambiguationData":[OSD([sQuery(id+"F6.wireOp",EDGE,"E30.rect.left"),sQuery(id+"F6.wireOp",EDGE,"E32.rect.top")])]})});
            var Q68;
            Q68=makeQuery(id+"F7.boolean.opBoolean","COPY",EDGE,{"derivedFrom":makeQuery(id+"F7.opExtrude","SWEPT_EDGE",EDGE,{"disambiguationData":[OSD([sQuery(id+"F6.wireOp",EDGE,"E30.rect.left"),sQuery(id+"F6.wireOp",EDGE,"E32.rect.bottom")])]})});
            var Q69;
            Q69=makeQuery(id+"F7.boolean.opBoolean","COPY",EDGE,{"derivedFrom":makeQuery(id+"F7.opExtrude","SWEPT_EDGE",EDGE,{"disambiguationData":[OSD([sQuery(id+"F6.wireOp",EDGE,"E30.rect.bottom"),sQuery(id+"F6.wireOp",EDGE,"E31.rect.right")])]})});
            var Q70;
            Q70=makeQuery(id+"F7.boolean.opBoolean","COPY",EDGE,{"derivedFrom":makeQuery(id+"F7.opExtrude","SWEPT_EDGE",EDGE,{"disambiguationData":[OSD([sQuery(id+"F6.wireOp",EDGE,"E30.rect.bottom"),sQuery(id+"F6.wireOp",EDGE,"E31.rect.left")])]})});
            var Q71;
            Q71=makeQuery(id+"F7.boolean.opBoolean","COPY",EDGE,{"derivedFrom":makeQuery(id+"F7.opExtrude","SWEPT_EDGE",EDGE,{"disambiguationData":[OSD([sQuery(id+"F6.wireOp",EDGE,"E30.rect.right"),sQuery(id+"F6.wireOp",EDGE,"E32.rect.top")])]})});
            var Q72;
            Q72=makeQuery(id+"F5.boolean.opBoolean","COPY",EDGE,{"derivedFrom":makeQuery(id+"F5.boolean.toolComplement.opBoolean","COPY",EDGE,{"derivedFrom":makeQuery(id+"F5.opPattern","COPY",EDGE,{"derivedFrom":makeQuery(id+"F3.boolean.opBoolean","COPY",EDGE,{"derivedFrom":makeQuery(id+"F3.opExtrude","CAP_EDGE",EDGE,{"disambiguationData":[OSD([sQuery(id+"F2.wireOp",EDGE,"E24.0")])],"isStart":true})}),"instanceName":"1"})})});
            var Q73;
            Q73=makeQuery(id+"F5.boolean.opBoolean","COPY",EDGE,{"derivedFrom":makeQuery(id+"F5.boolean.toolComplement.opBoolean","COPY",EDGE,{"derivedFrom":makeQuery(id+"F5.opPattern","COPY",EDGE,{"derivedFrom":makeQuery(id+"F3.boolean.opBoolean","COPY",EDGE,{"derivedFrom":makeQuery(id+"F3.opExtrude","CAP_EDGE",EDGE,{"disambiguationData":[OSD([sQuery(id+"F2.wireOp",EDGE,"E27.MirrorC")])],"isStart":true})}),"instanceName":"1"})})});
            var Q74;
            Q74=makeQuery(id+"F5.boolean.opBoolean","COPY",EDGE,{"derivedFrom":makeQuery(id+"F5.boolean.toolComplement.opBoolean","COPY",EDGE,{"derivedFrom":makeQuery(id+"F5.opPattern","COPY",EDGE,{"derivedFrom":makeQuery(id+"F3.boolean.opBoolean","COPY",EDGE,{"derivedFrom":makeQuery(id+"F3.opExtrude","CAP_EDGE",EDGE,{"disambiguationData":[OSD([sQuery(id+"F2.wireOp",EDGE,"E28.MirrorC")])],"isStart":true})}),"instanceName":"1"})})});
            var Q75;
            Q75=makeQuery(id+"F5.boolean.opBoolean","COPY",EDGE,{"derivedFrom":makeQuery(id+"F5.boolean.toolComplement.opBoolean","COPY",EDGE,{"derivedFrom":makeQuery(id+"F5.opPattern","COPY",EDGE,{"derivedFrom":makeQuery(id+"F3.boolean.opBoolean","COPY",EDGE,{"derivedFrom":makeQuery(id+"F3.opExtrude","CAP_EDGE",EDGE,{"disambiguationData":[OSD([sQuery(id+"F2.wireOp",EDGE,"E29.MirrorC")])],"isStart":true})}),"instanceName":"1"})})});
            var Q76;
            Q76=makeQuery(id+"F5.boolean.opBoolean","COPY",EDGE,{"derivedFrom":makeQuery(id+"F5.boolean.toolComplement.opBoolean","COPY",EDGE,{"derivedFrom":makeQuery(id+"F5.opPattern","COPY",EDGE,{"derivedFrom":makeQuery(id+"F3.boolean.opBoolean","INTERSECT",EDGE,{"derivedFrom":[makeQuery(id+"F1.opExtrude","SWEPT_FACE",FACE,{"disambiguationData":[OSD([sQuery(id+"F0.wireOp",EDGE,"E10.MirrorC")])]}),makeQuery(id+"F3.opExtrude","CAP_FACE",FACE,{"disambiguationData":[OSD([sQuery(id+"F2.wireOp",EDGE,"E29.MirrorC")])],"isStart":false})]}),"instanceName":"1"})})});
            var Q77;
            Q77=makeQuery(id+"F5.boolean.opBoolean","COPY",EDGE,{"derivedFrom":makeQuery(id+"F5.boolean.toolComplement.opBoolean","COPY",EDGE,{"derivedFrom":makeQuery(id+"F5.opPattern","COPY",EDGE,{"derivedFrom":makeQuery(id+"F3.boolean.opBoolean","INTERSECT",EDGE,{"derivedFrom":[makeQuery(id+"F1.opExtrude","SWEPT_FACE",FACE,{"disambiguationData":[OSD([sQuery(id+"F0.wireOp",EDGE,"E7")])]}),makeQuery(id+"F3.opExtrude","CAP_FACE",FACE,{"disambiguationData":[OSD([sQuery(id+"F2.wireOp",EDGE,"E28.MirrorC")])],"isStart":false})]}),"instanceName":"1"})})});
            var Q78;
            Q78=makeQuery(id+"F5.boolean.opBoolean","COPY",EDGE,{"derivedFrom":makeQuery(id+"F5.boolean.toolComplement.opBoolean","COPY",EDGE,{"derivedFrom":makeQuery(id+"F5.opPattern","COPY",EDGE,{"derivedFrom":makeQuery(id+"F3.boolean.opBoolean","INTERSECT",EDGE,{"derivedFrom":[makeQuery(id+"F1.opExtrude","SWEPT_FACE",FACE,{"disambiguationData":[OSD([sQuery(id+"F0.wireOp",EDGE,"E8.MirrorC")])]}),makeQuery(id+"F3.opExtrude","CAP_FACE",FACE,{"disambiguationData":[OSD([sQuery(id+"F2.wireOp",EDGE,"E27.MirrorC")])],"isStart":false})]}),"instanceName":"1"})})});
            var Q79;
            Q79=makeQuery(id+"F5.boolean.opBoolean","COPY",EDGE,{"derivedFrom":makeQuery(id+"F5.boolean.toolComplement.opBoolean","COPY",EDGE,{"derivedFrom":makeQuery(id+"F5.opPattern","COPY",EDGE,{"derivedFrom":makeQuery(id+"F3.boolean.opBoolean","COPY",EDGE,{"derivedFrom":makeQuery(id+"F3.opExtrude","CAP_EDGE",EDGE,{"disambiguationData":[OSD([sQuery(id+"F2.wireOp",EDGE,"E23.0")])],"isStart":false})}),"instanceName":"1"})})});
            var Q80;
            Q80=makeQuery(id+"F3.boolean.opBoolean","COPY",EDGE,{"derivedFrom":makeQuery(id+"F3.opExtrude","CAP_EDGE",EDGE,{"disambiguationData":[OSD([sQuery(id+"F2.wireOp",EDGE,"E24.0")])],"isStart":true})});
            var Q81;
            Q81=makeQuery(id+"F3.boolean.opBoolean","COPY",EDGE,{"derivedFrom":makeQuery(id+"F3.opExtrude","CAP_EDGE",EDGE,{"disambiguationData":[OSD([sQuery(id+"F2.wireOp",EDGE,"E23.0")])],"isStart":false})});
            var Q82;
            Q82=makeQuery(id+"F3.boolean.opBoolean","COPY",EDGE,{"derivedFrom":makeQuery(id+"F3.opExtrude","CAP_EDGE",EDGE,{"disambiguationData":[OSD([sQuery(id+"F2.wireOp",EDGE,"E29.MirrorC")])],"isStart":true})});
            var Q83;
            Q83=makeQuery(id+"F3.boolean.opBoolean","COPY",EDGE,{"derivedFrom":makeQuery(id+"F3.opExtrude","CAP_EDGE",EDGE,{"disambiguationData":[OSD([sQuery(id+"F2.wireOp",EDGE,"E27.MirrorC")])],"isStart":true})});
            var Q84;
            Q84=makeQuery(id+"F3.boolean.opBoolean","INTERSECT",EDGE,{"derivedFrom":[makeQuery(id+"F1.opExtrude","SWEPT_FACE",FACE,{"disambiguationData":[OSD([sQuery(id+"F0.wireOp",EDGE,"E8.MirrorC")])]}),makeQuery(id+"F3.opExtrude","CAP_FACE",FACE,{"disambiguationData":[OSD([sQuery(id+"F2.wireOp",EDGE,"E27.MirrorC")])],"isStart":false})]});
            var Q85;
            Q85=makeQuery(id+"F3.boolean.opBoolean","COPY",EDGE,{"derivedFrom":makeQuery(id+"F3.opExtrude","CAP_EDGE",EDGE,{"disambiguationData":[OSD([sQuery(id+"F2.wireOp",EDGE,"E28.MirrorC")])],"isStart":true})});
            var Q86;
            Q86=makeQuery(id+"F3.boolean.opBoolean","INTERSECT",EDGE,{"derivedFrom":[makeQuery(id+"F1.opExtrude","SWEPT_FACE",FACE,{"disambiguationData":[OSD([sQuery(id+"F0.wireOp",EDGE,"E10.MirrorC")])]}),makeQuery(id+"F3.opExtrude","CAP_FACE",FACE,{"disambiguationData":[OSD([sQuery(id+"F2.wireOp",EDGE,"E29.MirrorC")])],"isStart":false})]});
            var Q87;
            Q87=makeQuery(id+"F3.boolean.opBoolean","INTERSECT",EDGE,{"derivedFrom":[makeQuery(id+"F1.opExtrude","SWEPT_FACE",FACE,{"disambiguationData":[OSD([sQuery(id+"F0.wireOp",EDGE,"E7")])]}),makeQuery(id+"F3.opExtrude","CAP_FACE",FACE,{"disambiguationData":[OSD([sQuery(id+"F2.wireOp",EDGE,"E28.MirrorC")])],"isStart":false})]});
            fillet(context, id + "F9", {"entities" : qUnion([Q0, Q1, Q2, Q3, Q4, Q5, Q6, Q7, Q8, Q9, Q10, Q11, Q12, Q13, Q14, Q15, Q16, Q17, Q18, Q19, Q20, Q21, Q22, Q23, Q24, Q25, Q26, Q27, Q28, Q29, Q30, Q31, Q32, Q33, Q34, Q35, Q36, Q37, Q38, Q39, Q40, Q41, Q42, Q43, Q44, Q45, Q46, Q47, Q48, Q49, Q50, Q51, Q52, Q53, Q54, Q55, Q56, Q57, Q58, Q59, Q60, Q61, Q62, Q63, Q64, Q65, Q66, Q67, Q68, Q69, Q70, Q71, Q72, Q73, Q74, Q75, Q76, Q77, Q78, Q79, Q80, Q81, Q82, Q83, Q84, Q85, Q86, Q87]), "radius" : 0.1 * mm, "allowEdgeOverflow" : false});
        }
    });
